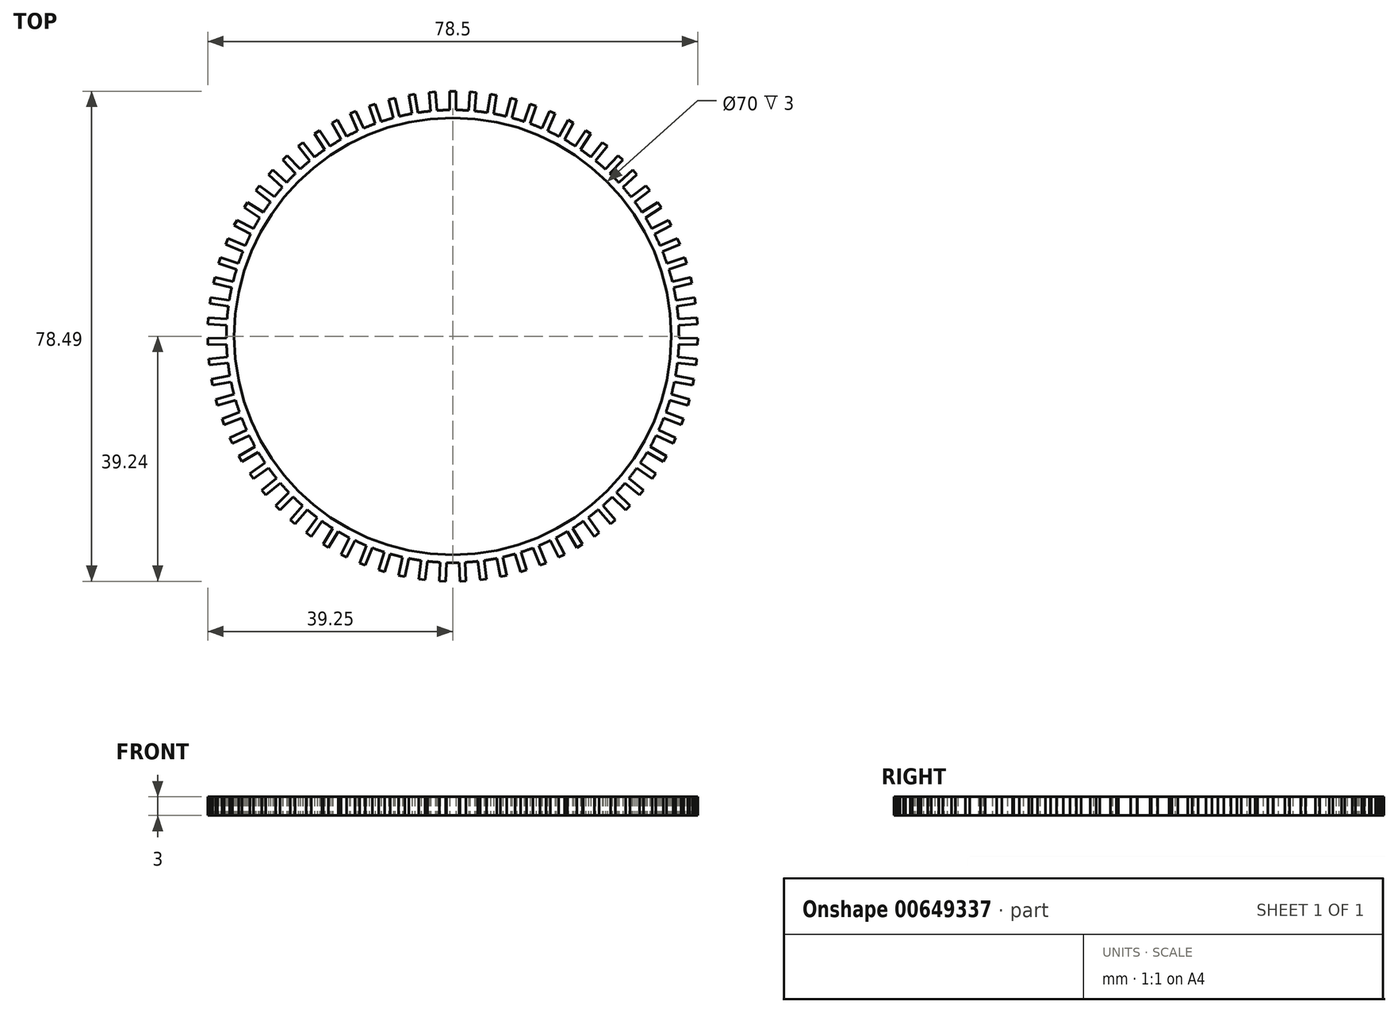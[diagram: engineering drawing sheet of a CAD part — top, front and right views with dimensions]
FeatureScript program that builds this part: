
annotation { "Feature Type Name" : "Feature", "Feature Type Description" : "" }
export const myFeature = defineFeature(function(context is Context, id is Id, definition is map)
    precondition{}
    {
        {
            var Q0;
            Q0=qCreatedBy(makeId("Top.planeOp"),FACE);
            var sketch = newSketch(context, id + "F0", { "sketchPlane" : qUnion([Q0])});
            skCircle(sketch, "E0", {"center": v(0, 0) * mm, "radius": 36.25 * mm});
            skCircle(sketch, "E1", {"center": v(0, 0) * mm, "radius": 35 * mm});
            skLineSegment(sketch, "E2.bottom", {"start": v(0.5, 39.25) * mm, "end": v(-0.5, 39.25) * mm});
            skLineSegment(sketch, "E2.top", {"start": v(0.5, 33.25) * mm, "end": v(-0.5, 33.25) * mm});
            skLineSegment(sketch, "E2.left", {"start": v(0.5, 39.25) * mm, "end": v(0.5, 33.25) * mm});
            skLineSegment(sketch, "E2.right", {"start": v(-0.5, 39.25) * mm, "end": v(-0.5, 33.25) * mm});
            skPoint(sketch, "E2.middle", {"position": v(0, 36.25) * mm});
            skLineSegment(sketch, "E3.1.0", {"start": v(-2.79, 39.15) * mm, "end": v(-3.78, 39.07) * mm});
            skLineSegment(sketch, "E3.1.1", {"start": v(-3.78, 39.07) * mm, "end": v(-3.28, 33.1) * mm});
            skLineSegment(sketch, "E3.1.2", {"start": v(-2.79, 39.15) * mm, "end": v(-2.28, 33.18) * mm});
            skLineSegment(sketch, "E3.2.0", {"start": v(-6.05, 38.78) * mm, "end": v(-7.04, 38.62) * mm});
            skLineSegment(sketch, "E3.2.1", {"start": v(-7.04, 38.62) * mm, "end": v(-6.04, 32.7) * mm});
            skLineSegment(sketch, "E3.2.2", {"start": v(-6.05, 38.78) * mm, "end": v(-5.05, 32.87) * mm});
            skLineSegment(sketch, "E3.3.0", {"start": v(-9.28, 38.14) * mm, "end": v(-10.25, 37.9) * mm});
            skLineSegment(sketch, "E3.3.1", {"start": v(-10.25, 37.9) * mm, "end": v(-8.75, 32.08) * mm});
            skLineSegment(sketch, "E3.3.2", {"start": v(-9.28, 38.14) * mm, "end": v(-7.78, 32.33) * mm});
            skLineSegment(sketch, "E3.4.0", {"start": v(-12.44, 37.23) * mm, "end": v(-13.38, 36.9) * mm});
            skLineSegment(sketch, "E3.4.1", {"start": v(-13.38, 36.9) * mm, "end": v(-11.4, 31.24) * mm});
            skLineSegment(sketch, "E3.4.2", {"start": v(-12.44, 37.23) * mm, "end": v(-10.46, 31.56) * mm});
            skLineSegment(sketch, "E3.5.0", {"start": v(-15.5, 36.06) * mm, "end": v(-16.42, 35.65) * mm});
            skLineSegment(sketch, "E3.5.1", {"start": v(-16.42, 35.65) * mm, "end": v(-13.98, 30.17) * mm});
            skLineSegment(sketch, "E3.5.2", {"start": v(-15.5, 36.06) * mm, "end": v(-13.07, 30.58) * mm});
            skLineSegment(sketch, "E3.6.0", {"start": v(-18.47, 34.64) * mm, "end": v(-19.35, 34.15) * mm});
            skLineSegment(sketch, "E3.6.1", {"start": v(-19.35, 34.15) * mm, "end": v(-16.46, 28.9) * mm});
            skLineSegment(sketch, "E3.6.2", {"start": v(-18.47, 34.64) * mm, "end": v(-15.58, 29.38) * mm});
            skLineSegment(sketch, "E3.7.0", {"start": v(-21.3, 32.97) * mm, "end": v(-22.14, 32.42) * mm});
            skLineSegment(sketch, "E3.7.1", {"start": v(-22.14, 32.42) * mm, "end": v(-18.82, 27.42) * mm});
            skLineSegment(sketch, "E3.7.2", {"start": v(-21.3, 32.97) * mm, "end": v(-17.98, 27.97) * mm});
            skLineSegment(sketch, "E3.8.0", {"start": v(-23.99, 31.07) * mm, "end": v(-24.77, 30.45) * mm});
            skLineSegment(sketch, "E3.8.1", {"start": v(-24.77, 30.45) * mm, "end": v(-21.05, 25.75) * mm});
            skLineSegment(sketch, "E3.8.2", {"start": v(-23.99, 31.07) * mm, "end": v(-20.26, 26.37) * mm});
            skLineSegment(sketch, "E3.9.0", {"start": v(-26.5, 28.95) * mm, "end": v(-27.23, 28.27) * mm});
            skLineSegment(sketch, "E3.9.1", {"start": v(-27.23, 28.27) * mm, "end": v(-23.13, 23.9) * mm});
            skLineSegment(sketch, "E3.9.2", {"start": v(-26.5, 28.95) * mm, "end": v(-22.4, 24.58) * mm});
            skLineSegment(sketch, "E3.10.0", {"start": v(-28.83, 26.63) * mm, "end": v(-29.5, 25.9) * mm});
            skLineSegment(sketch, "E3.10.1", {"start": v(-29.5, 25.9) * mm, "end": v(-25.04, 21.88) * mm});
            skLineSegment(sketch, "E3.10.2", {"start": v(-28.83, 26.63) * mm, "end": v(-24.38, 22.62) * mm});
            skLineSegment(sketch, "E3.11.0", {"start": v(-30.96, 24.13) * mm, "end": v(-31.57, 23.33) * mm});
            skLineSegment(sketch, "E3.11.1", {"start": v(-31.57, 23.33) * mm, "end": v(-26.79, 19.7) * mm});
            skLineSegment(sketch, "E3.11.2", {"start": v(-30.96, 24.13) * mm, "end": v(-26.18, 20.5) * mm});
            skLineSegment(sketch, "E3.12.0", {"start": v(-32.87, 21.45) * mm, "end": v(-33.4, 20.6) * mm});
            skLineSegment(sketch, "E3.12.1", {"start": v(-33.4, 20.6) * mm, "end": v(-28.34, 17.4) * mm});
            skLineSegment(sketch, "E3.12.2", {"start": v(-32.87, 21.45) * mm, "end": v(-27.8, 18.24) * mm});
            skLineSegment(sketch, "E3.13.0", {"start": v(-34.55, 18.63) * mm, "end": v(-35.02, 17.74) * mm});
            skLineSegment(sketch, "E3.13.1", {"start": v(-35.02, 17.74) * mm, "end": v(-29.7, 14.96) * mm});
            skLineSegment(sketch, "E3.13.2", {"start": v(-34.55, 18.63) * mm, "end": v(-29.23, 15.85) * mm});
            skLineSegment(sketch, "E3.14.0", {"start": v(-35.99, 15.67) * mm, "end": v(-36.38, 14.75) * mm});
            skLineSegment(sketch, "E3.14.1", {"start": v(-36.38, 14.75) * mm, "end": v(-30.85, 12.42) * mm});
            skLineSegment(sketch, "E3.14.2", {"start": v(-35.99, 15.67) * mm, "end": v(-30.46, 13.35) * mm});
            skLineSegment(sketch, "E3.15.0", {"start": v(-37.17, 12.6) * mm, "end": v(-37.48, 11.65) * mm});
            skLineSegment(sketch, "E3.15.1", {"start": v(-37.48, 11.65) * mm, "end": v(-31.78, 9.8) * mm});
            skLineSegment(sketch, "E3.15.2", {"start": v(-37.17, 12.6) * mm, "end": v(-31.47, 10.75) * mm});
            skLineSegment(sketch, "E3.16.0", {"start": v(-38.1, 9.45) * mm, "end": v(-38.33, 8.48) * mm});
            skLineSegment(sketch, "E3.16.1", {"start": v(-38.33, 8.48) * mm, "end": v(-32.49, 7.1) * mm});
            skLineSegment(sketch, "E3.16.2", {"start": v(-38.1, 9.45) * mm, "end": v(-32.26, 8.08) * mm});
            skLineSegment(sketch, "E3.17.0", {"start": v(-38.76, 6.23) * mm, "end": v(-38.9, 5.24) * mm});
            skLineSegment(sketch, "E3.17.1", {"start": v(-38.9, 5.24) * mm, "end": v(-32.97, 4.36) * mm});
            skLineSegment(sketch, "E3.17.2", {"start": v(-38.76, 6.23) * mm, "end": v(-32.82, 5.35) * mm});
            skLineSegment(sketch, "E3.18.0", {"start": v(-39.14, 2.96) * mm, "end": v(-39.2, 1.97) * mm});
            skLineSegment(sketch, "E3.18.1", {"start": v(-39.2, 1.97) * mm, "end": v(-33.22, 1.59) * mm});
            skLineSegment(sketch, "E3.18.2", {"start": v(-39.14, 2.96) * mm, "end": v(-33.15, 2.59) * mm});
            skLineSegment(sketch, "E3.19.0", {"start": v(-39.25, -0.32) * mm, "end": v(-39.23, -1.32) * mm});
            skLineSegment(sketch, "E3.19.1", {"start": v(-39.23, -1.32) * mm, "end": v(-33.23, -1.2) * mm});
            skLineSegment(sketch, "E3.19.2", {"start": v(-39.25, -0.32) * mm, "end": v(-33.25, -0.2) * mm});
            skLineSegment(sketch, "E3.20.0", {"start": v(-39.09, -3.6) * mm, "end": v(-38.98, -4.6) * mm});
            skLineSegment(sketch, "E3.20.1", {"start": v(-38.98, -4.6) * mm, "end": v(-33.02, -3.97) * mm});
            skLineSegment(sketch, "E3.20.2", {"start": v(-39.09, -3.6) * mm, "end": v(-33.12, -2.98) * mm});
            skLineSegment(sketch, "E3.21.0", {"start": v(-38.65, -6.86) * mm, "end": v(-38.46, -7.85) * mm});
            skLineSegment(sketch, "E3.21.1", {"start": v(-38.46, -7.85) * mm, "end": v(-32.57, -6.72) * mm});
            skLineSegment(sketch, "E3.21.2", {"start": v(-38.65, -6.86) * mm, "end": v(-32.75, -5.74) * mm});
            skLineSegment(sketch, "E3.22.0", {"start": v(-37.94, -10.07) * mm, "end": v(-37.67, -11.04) * mm});
            skLineSegment(sketch, "E3.22.1", {"start": v(-37.67, -11.04) * mm, "end": v(-31.9, -9.42) * mm});
            skLineSegment(sketch, "E3.22.2", {"start": v(-37.94, -10.07) * mm, "end": v(-32.16, -8.46) * mm});
            skLineSegment(sketch, "E3.23.0", {"start": v(-36.96, -13.21) * mm, "end": v(-36.61, -14.15) * mm});
            skLineSegment(sketch, "E3.23.1", {"start": v(-36.61, -14.15) * mm, "end": v(-31, -12.06) * mm});
            skLineSegment(sketch, "E3.23.2", {"start": v(-36.96, -13.21) * mm, "end": v(-31.34, -11.12) * mm});
            skLineSegment(sketch, "E3.24.0", {"start": v(-35.73, -16.26) * mm, "end": v(-35.3, -17.16) * mm});
            skLineSegment(sketch, "E3.24.1", {"start": v(-35.3, -17.16) * mm, "end": v(-29.87, -14.6) * mm});
            skLineSegment(sketch, "E3.24.2", {"start": v(-35.73, -16.26) * mm, "end": v(-30.3, -13.7) * mm});
            skLineSegment(sketch, "E3.25.0", {"start": v(-34.24, -19.2) * mm, "end": v(-33.74, -20.06) * mm});
            skLineSegment(sketch, "E3.25.1", {"start": v(-33.74, -20.06) * mm, "end": v(-28.55, -17.06) * mm});
            skLineSegment(sketch, "E3.25.2", {"start": v(-34.24, -19.2) * mm, "end": v(-29.05, -16.2) * mm});
            skLineSegment(sketch, "E3.26.0", {"start": v(-32.52, -21.99) * mm, "end": v(-31.94, -22.81) * mm});
            skLineSegment(sketch, "E3.26.1", {"start": v(-31.94, -22.81) * mm, "end": v(-27.02, -19.39) * mm});
            skLineSegment(sketch, "E3.26.2", {"start": v(-32.52, -21.99) * mm, "end": v(-27.59, -18.57) * mm});
            skLineSegment(sketch, "E3.27.0", {"start": v(-30.56, -24.63) * mm, "end": v(-29.92, -25.4) * mm});
            skLineSegment(sketch, "E3.27.1", {"start": v(-29.92, -25.4) * mm, "end": v(-25.3, -21.58) * mm});
            skLineSegment(sketch, "E3.27.2", {"start": v(-30.56, -24.63) * mm, "end": v(-25.94, -20.8) * mm});
            skLineSegment(sketch, "E3.28.0", {"start": v(-28.4, -27.1) * mm, "end": v(-27.7, -27.82) * mm});
            skLineSegment(sketch, "E3.28.1", {"start": v(-27.7, -27.82) * mm, "end": v(-23.4, -23.62) * mm});
            skLineSegment(sketch, "E3.28.2", {"start": v(-28.4, -27.1) * mm, "end": v(-24.1, -22.9) * mm});
            skLineSegment(sketch, "E3.29.0", {"start": v(-26.03, -29.39) * mm, "end": v(-25.27, -30.04) * mm});
            skLineSegment(sketch, "E3.29.1", {"start": v(-25.27, -30.04) * mm, "end": v(-21.35, -25.5) * mm});
            skLineSegment(sketch, "E3.29.2", {"start": v(-26.03, -29.39) * mm, "end": v(-22.1, -24.84) * mm});
            skLineSegment(sketch, "E3.30.0", {"start": v(-23.48, -31.46) * mm, "end": v(-22.67, -32.05) * mm});
            skLineSegment(sketch, "E3.30.1", {"start": v(-22.67, -32.05) * mm, "end": v(-19.14, -27.2) * mm});
            skLineSegment(sketch, "E3.30.2", {"start": v(-23.48, -31.46) * mm, "end": v(-19.95, -26.6) * mm});
            skLineSegment(sketch, "E3.31.0", {"start": v(-20.76, -33.31) * mm, "end": v(-19.9, -33.83) * mm});
            skLineSegment(sketch, "E3.31.1", {"start": v(-19.9, -33.83) * mm, "end": v(-16.8, -28.7) * mm});
            skLineSegment(sketch, "E3.31.2", {"start": v(-20.76, -33.31) * mm, "end": v(-17.65, -28.18) * mm});
            skLineSegment(sketch, "E3.32.0", {"start": v(-17.9, -34.93) * mm, "end": v(-17, -35.38) * mm});
            skLineSegment(sketch, "E3.32.1", {"start": v(-17, -35.38) * mm, "end": v(-14.34, -30) * mm});
            skLineSegment(sketch, "E3.32.2", {"start": v(-17.9, -34.93) * mm, "end": v(-15.23, -29.56) * mm});
            skLineSegment(sketch, "E3.33.0", {"start": v(-14.91, -36.3) * mm, "end": v(-13.98, -36.68) * mm});
            skLineSegment(sketch, "E3.33.1", {"start": v(-13.98, -36.68) * mm, "end": v(-11.78, -31.1) * mm});
            skLineSegment(sketch, "E3.33.2", {"start": v(-14.91, -36.3) * mm, "end": v(-12.7, -30.73) * mm});
            skLineSegment(sketch, "E3.34.0", {"start": v(-11.82, -37.43) * mm, "end": v(-10.87, -37.72) * mm});
            skLineSegment(sketch, "E3.34.1", {"start": v(-10.87, -37.72) * mm, "end": v(-9.13, -31.98) * mm});
            skLineSegment(sketch, "E3.34.2", {"start": v(-11.82, -37.43) * mm, "end": v(-10.09, -31.69) * mm});
            skLineSegment(sketch, "E3.35.0", {"start": v(-8.65, -38.29) * mm, "end": v(-7.67, -38.5) * mm});
            skLineSegment(sketch, "E3.35.1", {"start": v(-7.67, -38.5) * mm, "end": v(-6.42, -32.63) * mm});
            skLineSegment(sketch, "E3.35.2", {"start": v(-8.65, -38.29) * mm, "end": v(-7.4, -32.42) * mm});
            skLineSegment(sketch, "E3.36.0", {"start": v(-5.42, -38.88) * mm, "end": v(-4.42, -39) * mm});
            skLineSegment(sketch, "E3.36.1", {"start": v(-4.42, -39) * mm, "end": v(-3.67, -33.05) * mm});
            skLineSegment(sketch, "E3.36.2", {"start": v(-5.42, -38.88) * mm, "end": v(-4.66, -32.93) * mm});
            skLineSegment(sketch, "E3.37.0", {"start": v(-2.14, -39.2) * mm, "end": v(-1.14, -39.24) * mm});
            skLineSegment(sketch, "E3.37.1", {"start": v(-1.14, -39.24) * mm, "end": v(-0.9, -33.24) * mm});
            skLineSegment(sketch, "E3.37.2", {"start": v(-2.14, -39.2) * mm, "end": v(-1.9, -33.2) * mm});
            skLineSegment(sketch, "E3.38.0", {"start": v(1.14, -39.24) * mm, "end": v(2.14, -39.2) * mm});
            skLineSegment(sketch, "E3.38.1", {"start": v(2.14, -39.2) * mm, "end": v(1.9, -33.2) * mm});
            skLineSegment(sketch, "E3.38.2", {"start": v(1.14, -39.24) * mm, "end": v(0.9, -33.24) * mm});
            skLineSegment(sketch, "E3.39.0", {"start": v(4.42, -39) * mm, "end": v(5.42, -38.88) * mm});
            skLineSegment(sketch, "E3.39.1", {"start": v(5.42, -38.88) * mm, "end": v(4.66, -32.93) * mm});
            skLineSegment(sketch, "E3.39.2", {"start": v(4.42, -39) * mm, "end": v(3.67, -33.05) * mm});
            skLineSegment(sketch, "E3.40.0", {"start": v(7.67, -38.5) * mm, "end": v(8.65, -38.29) * mm});
            skLineSegment(sketch, "E3.40.1", {"start": v(8.65, -38.29) * mm, "end": v(7.4, -32.42) * mm});
            skLineSegment(sketch, "E3.40.2", {"start": v(7.67, -38.5) * mm, "end": v(6.42, -32.63) * mm});
            skLineSegment(sketch, "E3.41.0", {"start": v(10.87, -37.72) * mm, "end": v(11.82, -37.43) * mm});
            skLineSegment(sketch, "E3.41.1", {"start": v(11.82, -37.43) * mm, "end": v(10.09, -31.69) * mm});
            skLineSegment(sketch, "E3.41.2", {"start": v(10.87, -37.72) * mm, "end": v(9.13, -31.98) * mm});
            skLineSegment(sketch, "E3.42.0", {"start": v(13.98, -36.68) * mm, "end": v(14.91, -36.3) * mm});
            skLineSegment(sketch, "E3.42.1", {"start": v(14.91, -36.3) * mm, "end": v(12.7, -30.73) * mm});
            skLineSegment(sketch, "E3.42.2", {"start": v(13.98, -36.68) * mm, "end": v(11.78, -31.1) * mm});
            skLineSegment(sketch, "E3.43.0", {"start": v(17, -35.38) * mm, "end": v(17.9, -34.93) * mm});
            skLineSegment(sketch, "E3.43.1", {"start": v(17.9, -34.93) * mm, "end": v(15.23, -29.56) * mm});
            skLineSegment(sketch, "E3.43.2", {"start": v(17, -35.38) * mm, "end": v(14.34, -30) * mm});
            skLineSegment(sketch, "E3.44.0", {"start": v(19.9, -33.83) * mm, "end": v(20.76, -33.31) * mm});
            skLineSegment(sketch, "E3.44.1", {"start": v(20.76, -33.31) * mm, "end": v(17.65, -28.18) * mm});
            skLineSegment(sketch, "E3.44.2", {"start": v(19.9, -33.83) * mm, "end": v(16.8, -28.7) * mm});
            skLineSegment(sketch, "E3.45.0", {"start": v(22.67, -32.05) * mm, "end": v(23.48, -31.46) * mm});
            skLineSegment(sketch, "E3.45.1", {"start": v(23.48, -31.46) * mm, "end": v(19.95, -26.6) * mm});
            skLineSegment(sketch, "E3.45.2", {"start": v(22.67, -32.05) * mm, "end": v(19.14, -27.2) * mm});
            skLineSegment(sketch, "E3.46.0", {"start": v(25.27, -30.04) * mm, "end": v(26.03, -29.39) * mm});
            skLineSegment(sketch, "E3.46.1", {"start": v(26.03, -29.39) * mm, "end": v(22.1, -24.84) * mm});
            skLineSegment(sketch, "E3.46.2", {"start": v(25.27, -30.04) * mm, "end": v(21.35, -25.5) * mm});
            skLineSegment(sketch, "E3.47.0", {"start": v(27.7, -27.82) * mm, "end": v(28.4, -27.1) * mm});
            skLineSegment(sketch, "E3.47.1", {"start": v(28.4, -27.1) * mm, "end": v(24.1, -22.9) * mm});
            skLineSegment(sketch, "E3.47.2", {"start": v(27.7, -27.82) * mm, "end": v(23.4, -23.62) * mm});
            skLineSegment(sketch, "E3.48.0", {"start": v(29.92, -25.4) * mm, "end": v(30.56, -24.63) * mm});
            skLineSegment(sketch, "E3.48.1", {"start": v(30.56, -24.63) * mm, "end": v(25.94, -20.8) * mm});
            skLineSegment(sketch, "E3.48.2", {"start": v(29.92, -25.4) * mm, "end": v(25.3, -21.58) * mm});
            skLineSegment(sketch, "E3.49.0", {"start": v(31.94, -22.81) * mm, "end": v(32.52, -21.99) * mm});
            skLineSegment(sketch, "E3.49.1", {"start": v(32.52, -21.99) * mm, "end": v(27.59, -18.57) * mm});
            skLineSegment(sketch, "E3.49.2", {"start": v(31.94, -22.81) * mm, "end": v(27.02, -19.39) * mm});
            skLineSegment(sketch, "E3.50.0", {"start": v(33.74, -20.06) * mm, "end": v(34.24, -19.2) * mm});
            skLineSegment(sketch, "E3.50.1", {"start": v(34.24, -19.2) * mm, "end": v(29.05, -16.2) * mm});
            skLineSegment(sketch, "E3.50.2", {"start": v(33.74, -20.06) * mm, "end": v(28.55, -17.06) * mm});
            skLineSegment(sketch, "E3.51.0", {"start": v(35.3, -17.16) * mm, "end": v(35.73, -16.26) * mm});
            skLineSegment(sketch, "E3.51.1", {"start": v(35.73, -16.26) * mm, "end": v(30.3, -13.7) * mm});
            skLineSegment(sketch, "E3.51.2", {"start": v(35.3, -17.16) * mm, "end": v(29.87, -14.6) * mm});
            skLineSegment(sketch, "E3.52.0", {"start": v(36.61, -14.15) * mm, "end": v(36.96, -13.21) * mm});
            skLineSegment(sketch, "E3.52.1", {"start": v(36.96, -13.21) * mm, "end": v(31.34, -11.12) * mm});
            skLineSegment(sketch, "E3.52.2", {"start": v(36.61, -14.15) * mm, "end": v(31, -12.06) * mm});
            skLineSegment(sketch, "E3.53.0", {"start": v(37.67, -11.04) * mm, "end": v(37.94, -10.07) * mm});
            skLineSegment(sketch, "E3.53.1", {"start": v(37.94, -10.07) * mm, "end": v(32.16, -8.46) * mm});
            skLineSegment(sketch, "E3.53.2", {"start": v(37.67, -11.04) * mm, "end": v(31.9, -9.42) * mm});
            skLineSegment(sketch, "E3.54.0", {"start": v(38.46, -7.85) * mm, "end": v(38.65, -6.86) * mm});
            skLineSegment(sketch, "E3.54.1", {"start": v(38.65, -6.86) * mm, "end": v(32.75, -5.74) * mm});
            skLineSegment(sketch, "E3.54.2", {"start": v(38.46, -7.85) * mm, "end": v(32.57, -6.72) * mm});
            skLineSegment(sketch, "E3.55.0", {"start": v(38.98, -4.6) * mm, "end": v(39.09, -3.6) * mm});
            skLineSegment(sketch, "E3.55.1", {"start": v(39.09, -3.6) * mm, "end": v(33.12, -2.98) * mm});
            skLineSegment(sketch, "E3.55.2", {"start": v(38.98, -4.6) * mm, "end": v(33.02, -3.97) * mm});
            skLineSegment(sketch, "E3.56.0", {"start": v(39.23, -1.32) * mm, "end": v(39.25, -0.32) * mm});
            skLineSegment(sketch, "E3.56.1", {"start": v(39.25, -0.32) * mm, "end": v(33.25, -0.2) * mm});
            skLineSegment(sketch, "E3.56.2", {"start": v(39.23, -1.32) * mm, "end": v(33.23, -1.2) * mm});
            skLineSegment(sketch, "E3.57.0", {"start": v(39.2, 1.97) * mm, "end": v(39.14, 2.96) * mm});
            skLineSegment(sketch, "E3.57.1", {"start": v(39.14, 2.96) * mm, "end": v(33.15, 2.59) * mm});
            skLineSegment(sketch, "E3.57.2", {"start": v(39.2, 1.97) * mm, "end": v(33.22, 1.59) * mm});
            skLineSegment(sketch, "E3.58.0", {"start": v(38.9, 5.24) * mm, "end": v(38.76, 6.23) * mm});
            skLineSegment(sketch, "E3.58.1", {"start": v(38.76, 6.23) * mm, "end": v(32.82, 5.35) * mm});
            skLineSegment(sketch, "E3.58.2", {"start": v(38.9, 5.24) * mm, "end": v(32.97, 4.36) * mm});
            skLineSegment(sketch, "E3.59.0", {"start": v(38.33, 8.48) * mm, "end": v(38.1, 9.45) * mm});
            skLineSegment(sketch, "E3.59.1", {"start": v(38.1, 9.45) * mm, "end": v(32.26, 8.08) * mm});
            skLineSegment(sketch, "E3.59.2", {"start": v(38.33, 8.48) * mm, "end": v(32.49, 7.1) * mm});
            skLineSegment(sketch, "E3.60.0", {"start": v(37.48, 11.65) * mm, "end": v(37.17, 12.6) * mm});
            skLineSegment(sketch, "E3.60.1", {"start": v(37.17, 12.6) * mm, "end": v(31.47, 10.75) * mm});
            skLineSegment(sketch, "E3.60.2", {"start": v(37.48, 11.65) * mm, "end": v(31.78, 9.8) * mm});
            skLineSegment(sketch, "E3.61.0", {"start": v(36.38, 14.75) * mm, "end": v(35.99, 15.67) * mm});
            skLineSegment(sketch, "E3.61.1", {"start": v(35.99, 15.67) * mm, "end": v(30.46, 13.35) * mm});
            skLineSegment(sketch, "E3.61.2", {"start": v(36.38, 14.75) * mm, "end": v(30.85, 12.42) * mm});
            skLineSegment(sketch, "E3.62.0", {"start": v(35.02, 17.74) * mm, "end": v(34.55, 18.63) * mm});
            skLineSegment(sketch, "E3.62.1", {"start": v(34.55, 18.63) * mm, "end": v(29.23, 15.85) * mm});
            skLineSegment(sketch, "E3.62.2", {"start": v(35.02, 17.74) * mm, "end": v(29.7, 14.96) * mm});
            skLineSegment(sketch, "E3.63.0", {"start": v(33.4, 20.6) * mm, "end": v(32.87, 21.45) * mm});
            skLineSegment(sketch, "E3.63.1", {"start": v(32.87, 21.45) * mm, "end": v(27.8, 18.24) * mm});
            skLineSegment(sketch, "E3.63.2", {"start": v(33.4, 20.6) * mm, "end": v(28.34, 17.4) * mm});
            skLineSegment(sketch, "E3.64.0", {"start": v(31.57, 23.33) * mm, "end": v(30.96, 24.13) * mm});
            skLineSegment(sketch, "E3.64.1", {"start": v(30.96, 24.13) * mm, "end": v(26.18, 20.5) * mm});
            skLineSegment(sketch, "E3.64.2", {"start": v(31.57, 23.33) * mm, "end": v(26.79, 19.7) * mm});
            skLineSegment(sketch, "E3.65.0", {"start": v(29.5, 25.9) * mm, "end": v(28.83, 26.63) * mm});
            skLineSegment(sketch, "E3.65.1", {"start": v(28.83, 26.63) * mm, "end": v(24.38, 22.62) * mm});
            skLineSegment(sketch, "E3.65.2", {"start": v(29.5, 25.9) * mm, "end": v(25.04, 21.88) * mm});
            skLineSegment(sketch, "E3.66.0", {"start": v(27.23, 28.27) * mm, "end": v(26.5, 28.95) * mm});
            skLineSegment(sketch, "E3.66.1", {"start": v(26.5, 28.95) * mm, "end": v(22.4, 24.58) * mm});
            skLineSegment(sketch, "E3.66.2", {"start": v(27.23, 28.27) * mm, "end": v(23.13, 23.9) * mm});
            skLineSegment(sketch, "E3.67.0", {"start": v(24.77, 30.45) * mm, "end": v(23.99, 31.07) * mm});
            skLineSegment(sketch, "E3.67.1", {"start": v(23.99, 31.07) * mm, "end": v(20.26, 26.37) * mm});
            skLineSegment(sketch, "E3.67.2", {"start": v(24.77, 30.45) * mm, "end": v(21.05, 25.75) * mm});
            skLineSegment(sketch, "E3.68.0", {"start": v(22.14, 32.42) * mm, "end": v(21.3, 32.97) * mm});
            skLineSegment(sketch, "E3.68.1", {"start": v(21.3, 32.97) * mm, "end": v(17.98, 27.97) * mm});
            skLineSegment(sketch, "E3.68.2", {"start": v(22.14, 32.42) * mm, "end": v(18.82, 27.42) * mm});
            skLineSegment(sketch, "E3.69.0", {"start": v(19.35, 34.15) * mm, "end": v(18.47, 34.64) * mm});
            skLineSegment(sketch, "E3.69.1", {"start": v(18.47, 34.64) * mm, "end": v(15.58, 29.38) * mm});
            skLineSegment(sketch, "E3.69.2", {"start": v(19.35, 34.15) * mm, "end": v(16.46, 28.9) * mm});
            skLineSegment(sketch, "E3.70.0", {"start": v(16.42, 35.65) * mm, "end": v(15.5, 36.06) * mm});
            skLineSegment(sketch, "E3.70.1", {"start": v(15.5, 36.06) * mm, "end": v(13.07, 30.58) * mm});
            skLineSegment(sketch, "E3.70.2", {"start": v(16.42, 35.65) * mm, "end": v(13.98, 30.17) * mm});
            skLineSegment(sketch, "E3.71.0", {"start": v(13.38, 36.9) * mm, "end": v(12.44, 37.23) * mm});
            skLineSegment(sketch, "E3.71.1", {"start": v(12.44, 37.23) * mm, "end": v(10.46, 31.56) * mm});
            skLineSegment(sketch, "E3.71.2", {"start": v(13.38, 36.9) * mm, "end": v(11.4, 31.24) * mm});
            skLineSegment(sketch, "E3.72.0", {"start": v(10.25, 37.9) * mm, "end": v(9.28, 38.14) * mm});
            skLineSegment(sketch, "E3.72.1", {"start": v(9.28, 38.14) * mm, "end": v(7.78, 32.33) * mm});
            skLineSegment(sketch, "E3.72.2", {"start": v(10.25, 37.9) * mm, "end": v(8.75, 32.08) * mm});
            skLineSegment(sketch, "E3.73.0", {"start": v(7.04, 38.62) * mm, "end": v(6.05, 38.78) * mm});
            skLineSegment(sketch, "E3.73.1", {"start": v(6.05, 38.78) * mm, "end": v(5.05, 32.87) * mm});
            skLineSegment(sketch, "E3.73.2", {"start": v(7.04, 38.62) * mm, "end": v(6.04, 32.7) * mm});
            skLineSegment(sketch, "E3.74.0", {"start": v(3.78, 39.07) * mm, "end": v(2.79, 39.15) * mm});
            skLineSegment(sketch, "E3.74.1", {"start": v(2.79, 39.15) * mm, "end": v(2.28, 33.18) * mm});
            skLineSegment(sketch, "E3.74.2", {"start": v(3.78, 39.07) * mm, "end": v(3.28, 33.1) * mm});
            skCircle(sketch, "E4", {"center": v(0, 0) * mm, "radius": 41.25 * mm});
            skCircle(sketch, "E5", {"center": v(0, 0) * mm, "radius": 44.56 * mm});
            skSolve(sketch);
        }
        {
            var Q0;
            {var subQ0=sQuery(id+"F0.wireOp",EDGE,"E3.62.2");var subQ1=sQuery(id+"F0.wireOp",EDGE,"E1");var subQ2=makeQuery(id+"F0.imprint","INTERSECT",VERTEX,{"derivedFrom":[subQ1,subQ0]});Q0=makeQuery(id+"F0.imprint","IMPRINT",FACE,{"disambiguationData":[TD([[makeQuery(id+"F0.imprint","IMPRINT",EDGE,{"disambiguationData":[TD([[subQ2,-1.0]])],"derivedFrom":subQ1}),-1.0]])]});}
            var Q1;
            {var subQ0=sQuery(id+"F0.wireOp",EDGE,"E3.46.2");var subQ1=sQuery(id+"F0.wireOp",EDGE,"E1");var subQ2=makeQuery(id+"F0.imprint","INTERSECT",VERTEX,{"derivedFrom":[subQ1,subQ0]});Q1=makeQuery(id+"F0.imprint","IMPRINT",FACE,{"disambiguationData":[TD([[makeQuery(id+"F0.imprint","IMPRINT",EDGE,{"disambiguationData":[TD([[subQ2,-1.0]])],"derivedFrom":subQ1}),-1.0]])]});}
            var Q2;
            {var subQ0=sQuery(id+"F0.wireOp",EDGE,"E3.30.2");var subQ1=sQuery(id+"F0.wireOp",EDGE,"E1");var subQ2=makeQuery(id+"F0.imprint","INTERSECT",VERTEX,{"derivedFrom":[subQ1,subQ0]});Q2=makeQuery(id+"F0.imprint","IMPRINT",FACE,{"disambiguationData":[TD([[makeQuery(id+"F0.imprint","IMPRINT",EDGE,{"disambiguationData":[TD([[subQ2,-1.0]])],"derivedFrom":subQ1}),-1.0]])]});}
            var Q3;
            {var subQ0=sQuery(id+"F0.wireOp",EDGE,"E3.14.2");var subQ1=sQuery(id+"F0.wireOp",EDGE,"E1");var subQ2=makeQuery(id+"F0.imprint","INTERSECT",VERTEX,{"derivedFrom":[subQ1,subQ0]});Q3=makeQuery(id+"F0.imprint","IMPRINT",FACE,{"disambiguationData":[TD([[makeQuery(id+"F0.imprint","IMPRINT",EDGE,{"disambiguationData":[TD([[subQ2,-1.0]])],"derivedFrom":subQ1}),-1.0]])]});}
            var Q4;
            {var subQ0=sQuery(id+"F0.wireOp",EDGE,"E3.31.0");Q4=makeQuery(id+"F0.imprint","IMPRINT",FACE,{"disambiguationData":[TD([[makeQuery(id+"F0.imprint","IMPRINT",EDGE,{"derivedFrom":subQ0}),1.0]])]});}
            var Q5;
            {var subQ0=sQuery(id+"F0.wireOp",EDGE,"E3.95.0");Q5=makeQuery(id+"F0.imprint","IMPRINT",FACE,{"disambiguationData":[TD([[makeQuery(id+"F0.imprint","IMPRINT",EDGE,{"derivedFrom":subQ0}),1.0]])]});}
            var Q6;
            {var subQ0=sQuery(id+"F0.wireOp",EDGE,"E3.79.0");Q6=makeQuery(id+"F0.imprint","IMPRINT",FACE,{"disambiguationData":[TD([[makeQuery(id+"F0.imprint","IMPRINT",EDGE,{"derivedFrom":subQ0}),1.0]])]});}
            var Q7;
            {var subQ0=sQuery(id+"F0.wireOp",EDGE,"E3.63.0");Q7=makeQuery(id+"F0.imprint","IMPRINT",FACE,{"disambiguationData":[TD([[makeQuery(id+"F0.imprint","IMPRINT",EDGE,{"derivedFrom":subQ0}),1.0]])]});}
            var Q8;
            {var subQ0=sQuery(id+"F0.wireOp",EDGE,"E3.47.0");Q8=makeQuery(id+"F0.imprint","IMPRINT",FACE,{"disambiguationData":[TD([[makeQuery(id+"F0.imprint","IMPRINT",EDGE,{"derivedFrom":subQ0}),1.0]])]});}
            var Q9;
            {var subQ0=sQuery(id+"F0.wireOp",EDGE,"E3.33.1");var subQ1=sQuery(id+"F0.wireOp",EDGE,"E1");var subQ2=makeQuery(id+"F0.imprint","INTERSECT",VERTEX,{"derivedFrom":[subQ1,subQ0]});Q9=makeQuery(id+"F0.imprint","IMPRINT",FACE,{"disambiguationData":[TD([[makeQuery(id+"F0.imprint","IMPRINT",EDGE,{"disambiguationData":[TD([[subQ2,-1.0]])],"derivedFrom":subQ1}),-1.0]])]});}
            var Q10;
            {var subQ0=sQuery(id+"F0.wireOp",EDGE,"E3.17.1");var subQ1=sQuery(id+"F0.wireOp",EDGE,"E1");var subQ2=makeQuery(id+"F0.imprint","INTERSECT",VERTEX,{"derivedFrom":[subQ1,subQ0]});Q10=makeQuery(id+"F0.imprint","IMPRINT",FACE,{"disambiguationData":[TD([[makeQuery(id+"F0.imprint","IMPRINT",EDGE,{"disambiguationData":[TD([[subQ2,-1.0]])],"derivedFrom":subQ1}),-1.0]])]});}
            var Q11;
            {var subQ0=sQuery(id+"F0.wireOp",EDGE,"E3.85.1");var subQ1=sQuery(id+"F0.wireOp",EDGE,"E1");var subQ2=makeQuery(id+"F0.imprint","INTERSECT",VERTEX,{"derivedFrom":[subQ1,subQ0]});Q11=makeQuery(id+"F0.imprint","IMPRINT",FACE,{"disambiguationData":[TD([[makeQuery(id+"F0.imprint","IMPRINT",EDGE,{"disambiguationData":[TD([[subQ2,-1.0]])],"derivedFrom":subQ1}),-1.0]])]});}
            var Q12;
            {var subQ0=sQuery(id+"F0.wireOp",EDGE,"E3.82.2");var subQ1=sQuery(id+"F0.wireOp",EDGE,"E1");var subQ2=makeQuery(id+"F0.imprint","INTERSECT",VERTEX,{"derivedFrom":[subQ1,subQ0]});Q12=makeQuery(id+"F0.imprint","IMPRINT",FACE,{"disambiguationData":[TD([[makeQuery(id+"F0.imprint","IMPRINT",EDGE,{"disambiguationData":[TD([[subQ2,-1.0]])],"derivedFrom":subQ1}),-1.0]])]});}
            var Q13;
            {var subQ0=sQuery(id+"F0.wireOp",EDGE,"E3.65.1");var subQ1=sQuery(id+"F0.wireOp",EDGE,"E1");var subQ2=makeQuery(id+"F0.imprint","INTERSECT",VERTEX,{"derivedFrom":[subQ1,subQ0]});Q13=makeQuery(id+"F0.imprint","IMPRINT",FACE,{"disambiguationData":[TD([[makeQuery(id+"F0.imprint","IMPRINT",EDGE,{"disambiguationData":[TD([[subQ2,-1.0]])],"derivedFrom":subQ1}),-1.0]])]});}
            var Q14;
            {var subQ0=sQuery(id+"F0.wireOp",EDGE,"E3.49.1");var subQ1=sQuery(id+"F0.wireOp",EDGE,"E1");var subQ2=makeQuery(id+"F0.imprint","INTERSECT",VERTEX,{"derivedFrom":[subQ1,subQ0]});Q14=makeQuery(id+"F0.imprint","IMPRINT",FACE,{"disambiguationData":[TD([[makeQuery(id+"F0.imprint","IMPRINT",EDGE,{"disambiguationData":[TD([[subQ2,-1.0]])],"derivedFrom":subQ1}),-1.0]])]});}
            var Q15;
            {var subQ0=sQuery(id+"F0.wireOp",EDGE,"E3.77.0");Q15=makeQuery(id+"F0.imprint","IMPRINT",FACE,{"disambiguationData":[TD([[makeQuery(id+"F0.imprint","IMPRINT",EDGE,{"derivedFrom":subQ0}),1.0]])]});}
            var Q16;
            {var subQ0=sQuery(id+"F0.wireOp",EDGE,"E3.61.0");Q16=makeQuery(id+"F0.imprint","IMPRINT",FACE,{"disambiguationData":[TD([[makeQuery(id+"F0.imprint","IMPRINT",EDGE,{"derivedFrom":subQ0}),1.0]])]});}
            var Q17;
            {var subQ0=sQuery(id+"F0.wireOp",EDGE,"E3.45.0");Q17=makeQuery(id+"F0.imprint","IMPRINT",FACE,{"disambiguationData":[TD([[makeQuery(id+"F0.imprint","IMPRINT",EDGE,{"derivedFrom":subQ0}),1.0]])]});}
            var Q18;
            {var subQ0=sQuery(id+"F0.wireOp",EDGE,"E3.15.1");var subQ1=sQuery(id+"F0.wireOp",EDGE,"E1");var subQ2=makeQuery(id+"F0.imprint","INTERSECT",VERTEX,{"derivedFrom":[subQ1,subQ0]});Q18=makeQuery(id+"F0.imprint","IMPRINT",FACE,{"disambiguationData":[TD([[makeQuery(id+"F0.imprint","IMPRINT",EDGE,{"disambiguationData":[TD([[subQ2,-1.0]])],"derivedFrom":subQ1}),-1.0]])]});}
            var Q19;
            {var subQ0=sQuery(id+"F0.wireOp",EDGE,"E3.93.0");Q19=makeQuery(id+"F0.imprint","IMPRINT",FACE,{"disambiguationData":[TD([[makeQuery(id+"F0.imprint","IMPRINT",EDGE,{"derivedFrom":subQ0}),1.0]])]});}
            var Q20;
            {var subQ0=sQuery(id+"F0.wireOp",EDGE,"E3.47.1");var subQ1=sQuery(id+"F0.wireOp",EDGE,"E1");var subQ2=makeQuery(id+"F0.imprint","INTERSECT",VERTEX,{"derivedFrom":[subQ1,subQ0]});Q20=makeQuery(id+"F0.imprint","IMPRINT",FACE,{"disambiguationData":[TD([[makeQuery(id+"F0.imprint","IMPRINT",EDGE,{"disambiguationData":[TD([[subQ2,-1.0]])],"derivedFrom":subQ1}),-1.0]])]});}
            var Q21;
            {var subQ0=sQuery(id+"F0.wireOp",EDGE,"E3.31.1");var subQ1=sQuery(id+"F0.wireOp",EDGE,"E1");var subQ2=makeQuery(id+"F0.imprint","INTERSECT",VERTEX,{"derivedFrom":[subQ1,subQ0]});Q21=makeQuery(id+"F0.imprint","IMPRINT",FACE,{"disambiguationData":[TD([[makeQuery(id+"F0.imprint","IMPRINT",EDGE,{"disambiguationData":[TD([[subQ2,-1.0]])],"derivedFrom":subQ1}),-1.0]])]});}
            var Q22;
            {var subQ0=sQuery(id+"F0.wireOp",EDGE,"E3.96.2");var subQ1=sQuery(id+"F0.wireOp",EDGE,"E1");var subQ2=makeQuery(id+"F0.imprint","INTERSECT",VERTEX,{"derivedFrom":[subQ1,subQ0]});Q22=makeQuery(id+"F0.imprint","IMPRINT",FACE,{"disambiguationData":[TD([[makeQuery(id+"F0.imprint","IMPRINT",EDGE,{"disambiguationData":[TD([[subQ2,-1.0]])],"derivedFrom":subQ1}),-1.0]])]});}
            var Q23;
            {var subQ0=sQuery(id+"F0.wireOp",EDGE,"E3.78.0");Q23=makeQuery(id+"F0.imprint","IMPRINT",FACE,{"disambiguationData":[TD([[makeQuery(id+"F0.imprint","IMPRINT",EDGE,{"derivedFrom":subQ0}),1.0]])]});}
            var Q24;
            {var subQ0=sQuery(id+"F0.wireOp",EDGE,"E3.62.0");Q24=makeQuery(id+"F0.imprint","IMPRINT",FACE,{"disambiguationData":[TD([[makeQuery(id+"F0.imprint","IMPRINT",EDGE,{"derivedFrom":subQ0}),1.0]])]});}
            var Q25;
            {var subQ0=sQuery(id+"F0.wireOp",EDGE,"E3.30.0");Q25=makeQuery(id+"F0.imprint","IMPRINT",FACE,{"disambiguationData":[TD([[makeQuery(id+"F0.imprint","IMPRINT",EDGE,{"derivedFrom":subQ0}),1.0]])]});}
            var Q26;
            {var subQ0=sQuery(id+"F0.wireOp",EDGE,"E3.16.1");var subQ1=sQuery(id+"F0.wireOp",EDGE,"E1");var subQ2=makeQuery(id+"F0.imprint","INTERSECT",VERTEX,{"derivedFrom":[subQ1,subQ0]});Q26=makeQuery(id+"F0.imprint","IMPRINT",FACE,{"disambiguationData":[TD([[makeQuery(id+"F0.imprint","IMPRINT",EDGE,{"disambiguationData":[TD([[subQ2,-1.0]])],"derivedFrom":subQ1}),-1.0]])]});}
            var Q27;
            {var subQ0=sQuery(id+"F0.wireOp",EDGE,"E3.84.1");var subQ1=sQuery(id+"F0.wireOp",EDGE,"E1");var subQ2=makeQuery(id+"F0.imprint","INTERSECT",VERTEX,{"derivedFrom":[subQ1,subQ0]});Q27=makeQuery(id+"F0.imprint","IMPRINT",FACE,{"disambiguationData":[TD([[makeQuery(id+"F0.imprint","IMPRINT",EDGE,{"disambiguationData":[TD([[subQ2,-1.0]])],"derivedFrom":subQ1}),-1.0]])]});}
            var Q28;
            {var subQ0=sQuery(id+"F0.wireOp",EDGE,"E3.94.0");Q28=makeQuery(id+"F0.imprint","IMPRINT",FACE,{"disambiguationData":[TD([[makeQuery(id+"F0.imprint","IMPRINT",EDGE,{"derivedFrom":subQ0}),1.0]])]});}
            var Q29;
            {var subQ0=sQuery(id+"F0.wireOp",EDGE,"E3.64.1");var subQ1=sQuery(id+"F0.wireOp",EDGE,"E1");var subQ2=makeQuery(id+"F0.imprint","INTERSECT",VERTEX,{"derivedFrom":[subQ1,subQ0]});Q29=makeQuery(id+"F0.imprint","IMPRINT",FACE,{"disambiguationData":[TD([[makeQuery(id+"F0.imprint","IMPRINT",EDGE,{"disambiguationData":[TD([[subQ2,-1.0]])],"derivedFrom":subQ1}),-1.0]])]});}
            var Q30;
            {var subQ0=sQuery(id+"F0.wireOp",EDGE,"E3.32.1");var subQ1=sQuery(id+"F0.wireOp",EDGE,"E1");var subQ2=makeQuery(id+"F0.imprint","INTERSECT",VERTEX,{"derivedFrom":[subQ1,subQ0]});Q30=makeQuery(id+"F0.imprint","IMPRINT",FACE,{"disambiguationData":[TD([[makeQuery(id+"F0.imprint","IMPRINT",EDGE,{"disambiguationData":[TD([[subQ2,-1.0]])],"derivedFrom":subQ1}),-1.0]])]});}
            var Q31;
            {var subQ0=sQuery(id+"F0.wireOp",EDGE,"E3.45.2");var subQ1=sQuery(id+"F0.wireOp",EDGE,"E1");var subQ2=makeQuery(id+"F0.imprint","INTERSECT",VERTEX,{"derivedFrom":[subQ1,subQ0]});Q31=makeQuery(id+"F0.imprint","IMPRINT",FACE,{"disambiguationData":[TD([[makeQuery(id+"F0.imprint","IMPRINT",EDGE,{"disambiguationData":[TD([[subQ2,-1.0]])],"derivedFrom":subQ1}),-1.0]])]});}
            var Q32;
            {var subQ0=sQuery(id+"F0.wireOp",EDGE,"E3.29.2");var subQ1=sQuery(id+"F0.wireOp",EDGE,"E1");var subQ2=makeQuery(id+"F0.imprint","INTERSECT",VERTEX,{"derivedFrom":[subQ1,subQ0]});Q32=makeQuery(id+"F0.imprint","IMPRINT",FACE,{"disambiguationData":[TD([[makeQuery(id+"F0.imprint","IMPRINT",EDGE,{"disambiguationData":[TD([[subQ2,-1.0]])],"derivedFrom":subQ1}),-1.0]])]});}
            var Q33;
            {var subQ0=sQuery(id+"F0.wireOp",EDGE,"E3.13.2");var subQ1=sQuery(id+"F0.wireOp",EDGE,"E1");var subQ2=makeQuery(id+"F0.imprint","INTERSECT",VERTEX,{"derivedFrom":[subQ1,subQ0]});Q33=makeQuery(id+"F0.imprint","IMPRINT",FACE,{"disambiguationData":[TD([[makeQuery(id+"F0.imprint","IMPRINT",EDGE,{"disambiguationData":[TD([[subQ2,-1.0]])],"derivedFrom":subQ1}),-1.0]])]});}
            var Q34;
            {var subQ0=sQuery(id+"F0.wireOp",EDGE,"E3.97.2");var subQ1=sQuery(id+"F0.wireOp",EDGE,"E1");var subQ2=makeQuery(id+"F0.imprint","INTERSECT",VERTEX,{"derivedFrom":[subQ1,subQ0]});Q34=makeQuery(id+"F0.imprint","IMPRINT",FACE,{"disambiguationData":[TD([[makeQuery(id+"F0.imprint","IMPRINT",EDGE,{"disambiguationData":[TD([[subQ2,-1.0]])],"derivedFrom":subQ1}),-1.0]])]});}
            var Q35;
            {var subQ0=sQuery(id+"F0.wireOp",EDGE,"E3.16.0");Q35=makeQuery(id+"F0.imprint","IMPRINT",FACE,{"disambiguationData":[TD([[makeQuery(id+"F0.imprint","IMPRINT",EDGE,{"derivedFrom":subQ0}),1.0]])]});}
            var Q36;
            {var subQ0=sQuery(id+"F0.wireOp",EDGE,"E3.80.0");Q36=makeQuery(id+"F0.imprint","IMPRINT",FACE,{"disambiguationData":[TD([[makeQuery(id+"F0.imprint","IMPRINT",EDGE,{"derivedFrom":subQ0}),1.0]])]});}
            var Q37;
            {var subQ0=sQuery(id+"F0.wireOp",EDGE,"E3.64.0");Q37=makeQuery(id+"F0.imprint","IMPRINT",FACE,{"disambiguationData":[TD([[makeQuery(id+"F0.imprint","IMPRINT",EDGE,{"derivedFrom":subQ0}),1.0]])]});}
            var Q38;
            {var subQ0=sQuery(id+"F0.wireOp",EDGE,"E3.18.1");var subQ1=sQuery(id+"F0.wireOp",EDGE,"E1");var subQ2=makeQuery(id+"F0.imprint","INTERSECT",VERTEX,{"derivedFrom":[subQ1,subQ0]});Q38=makeQuery(id+"F0.imprint","IMPRINT",FACE,{"disambiguationData":[TD([[makeQuery(id+"F0.imprint","IMPRINT",EDGE,{"disambiguationData":[TD([[subQ2,-1.0]])],"derivedFrom":subQ1}),-1.0]])]});}
            var Q39;
            {var subQ0=sQuery(id+"F0.wireOp",EDGE,"E3.2.1");var subQ1=sQuery(id+"F0.wireOp",EDGE,"E1");var subQ2=makeQuery(id+"F0.imprint","INTERSECT",VERTEX,{"derivedFrom":[subQ1,subQ0]});Q39=makeQuery(id+"F0.imprint","IMPRINT",FACE,{"disambiguationData":[TD([[makeQuery(id+"F0.imprint","IMPRINT",EDGE,{"disambiguationData":[TD([[subQ2,-1.0]])],"derivedFrom":subQ1}),-1.0]])]});}
            var Q40;
            {var subQ0=sQuery(id+"F0.wireOp",EDGE,"E3.96.0");Q40=makeQuery(id+"F0.imprint","IMPRINT",FACE,{"disambiguationData":[TD([[makeQuery(id+"F0.imprint","IMPRINT",EDGE,{"derivedFrom":subQ0}),1.0]])]});}
            var Q41;
            {var subQ0=sQuery(id+"F0.wireOp",EDGE,"E3.66.1");var subQ1=sQuery(id+"F0.wireOp",EDGE,"E1");var subQ2=makeQuery(id+"F0.imprint","INTERSECT",VERTEX,{"derivedFrom":[subQ1,subQ0]});Q41=makeQuery(id+"F0.imprint","IMPRINT",FACE,{"disambiguationData":[TD([[makeQuery(id+"F0.imprint","IMPRINT",EDGE,{"disambiguationData":[TD([[subQ2,-1.0]])],"derivedFrom":subQ1}),-1.0]])]});}
            var Q42;
            {var subQ0=sQuery(id+"F0.wireOp",EDGE,"E3.50.1");var subQ1=sQuery(id+"F0.wireOp",EDGE,"E1");var subQ2=makeQuery(id+"F0.imprint","INTERSECT",VERTEX,{"derivedFrom":[subQ1,subQ0]});Q42=makeQuery(id+"F0.imprint","IMPRINT",FACE,{"disambiguationData":[TD([[makeQuery(id+"F0.imprint","IMPRINT",EDGE,{"disambiguationData":[TD([[subQ2,-1.0]])],"derivedFrom":subQ1}),-1.0]])]});}
            var Q43;
            {var subQ0=sQuery(id+"F0.wireOp",EDGE,"E3.34.1");var subQ1=sQuery(id+"F0.wireOp",EDGE,"E1");var subQ2=makeQuery(id+"F0.imprint","INTERSECT",VERTEX,{"derivedFrom":[subQ1,subQ0]});Q43=makeQuery(id+"F0.imprint","IMPRINT",FACE,{"disambiguationData":[TD([[makeQuery(id+"F0.imprint","IMPRINT",EDGE,{"disambiguationData":[TD([[subQ2,-1.0]])],"derivedFrom":subQ1}),-1.0]])]});}
            var Q44;
            {var subQ0=sQuery(id+"F0.wireOp",EDGE,"E3.99.2");var subQ1=sQuery(id+"F0.wireOp",EDGE,"E1");var subQ2=makeQuery(id+"F0.imprint","INTERSECT",VERTEX,{"derivedFrom":[subQ1,subQ0]});Q44=makeQuery(id+"F0.imprint","IMPRINT",FACE,{"disambiguationData":[TD([[makeQuery(id+"F0.imprint","IMPRINT",EDGE,{"disambiguationData":[TD([[subQ2,-1.0]])],"derivedFrom":subQ1}),-1.0]])]});}
            var Q45;
            {var subQ0=sQuery(id+"F0.wireOp",EDGE,"E3.17.0");Q45=makeQuery(id+"F0.imprint","IMPRINT",FACE,{"disambiguationData":[TD([[makeQuery(id+"F0.imprint","IMPRINT",EDGE,{"derivedFrom":subQ0}),1.0]])]});}
            var Q46;
            {var subQ0=sQuery(id+"F0.wireOp",EDGE,"E3.81.0");Q46=makeQuery(id+"F0.imprint","IMPRINT",FACE,{"disambiguationData":[TD([[makeQuery(id+"F0.imprint","IMPRINT",EDGE,{"derivedFrom":subQ0}),1.0]])]});}
            var Q47;
            {var subQ0=sQuery(id+"F0.wireOp",EDGE,"E3.65.0");Q47=makeQuery(id+"F0.imprint","IMPRINT",FACE,{"disambiguationData":[TD([[makeQuery(id+"F0.imprint","IMPRINT",EDGE,{"derivedFrom":subQ0}),1.0]])]});}
            var Q48;
            {var subQ0=sQuery(id+"F0.wireOp",EDGE,"E3.49.0");Q48=makeQuery(id+"F0.imprint","IMPRINT",FACE,{"disambiguationData":[TD([[makeQuery(id+"F0.imprint","IMPRINT",EDGE,{"derivedFrom":subQ0}),1.0]])]});}
            var Q49;
            {var subQ0=sQuery(id+"F0.wireOp",EDGE,"E3.19.1");var subQ1=sQuery(id+"F0.wireOp",EDGE,"E1");var subQ2=makeQuery(id+"F0.imprint","INTERSECT",VERTEX,{"derivedFrom":[subQ1,subQ0]});Q49=makeQuery(id+"F0.imprint","IMPRINT",FACE,{"disambiguationData":[TD([[makeQuery(id+"F0.imprint","IMPRINT",EDGE,{"disambiguationData":[TD([[subQ2,-1.0]])],"derivedFrom":subQ1}),-1.0]])]});}
            var Q50;
            {var subQ0=sQuery(id+"F0.wireOp",EDGE,"E3.3.1");var subQ1=sQuery(id+"F0.wireOp",EDGE,"E1");var subQ2=makeQuery(id+"F0.imprint","INTERSECT",VERTEX,{"derivedFrom":[subQ1,subQ0]});Q50=makeQuery(id+"F0.imprint","IMPRINT",FACE,{"disambiguationData":[TD([[makeQuery(id+"F0.imprint","IMPRINT",EDGE,{"disambiguationData":[TD([[subQ2,-1.0]])],"derivedFrom":subQ1}),-1.0]])]});}
            var Q51;
            {var subQ0=sQuery(id+"F0.wireOp",EDGE,"E3.87.1");var subQ1=sQuery(id+"F0.wireOp",EDGE,"E1");var subQ2=makeQuery(id+"F0.imprint","INTERSECT",VERTEX,{"derivedFrom":[subQ1,subQ0]});Q51=makeQuery(id+"F0.imprint","IMPRINT",FACE,{"disambiguationData":[TD([[makeQuery(id+"F0.imprint","IMPRINT",EDGE,{"disambiguationData":[TD([[subQ2,-1.0]])],"derivedFrom":subQ1}),-1.0]])]});}
            var Q52;
            {var subQ0=sQuery(id+"F0.wireOp",EDGE,"E3.97.0");Q52=makeQuery(id+"F0.imprint","IMPRINT",FACE,{"disambiguationData":[TD([[makeQuery(id+"F0.imprint","IMPRINT",EDGE,{"derivedFrom":subQ0}),1.0]])]});}
            var Q53;
            {var subQ0=sQuery(id+"F0.wireOp",EDGE,"E3.67.1");var subQ1=sQuery(id+"F0.wireOp",EDGE,"E1");var subQ2=makeQuery(id+"F0.imprint","INTERSECT",VERTEX,{"derivedFrom":[subQ1,subQ0]});Q53=makeQuery(id+"F0.imprint","IMPRINT",FACE,{"disambiguationData":[TD([[makeQuery(id+"F0.imprint","IMPRINT",EDGE,{"disambiguationData":[TD([[subQ2,-1.0]])],"derivedFrom":subQ1}),-1.0]])]});}
            var Q54;
            {var subQ0=sQuery(id+"F0.wireOp",EDGE,"E3.35.1");var subQ1=sQuery(id+"F0.wireOp",EDGE,"E1");var subQ2=makeQuery(id+"F0.imprint","INTERSECT",VERTEX,{"derivedFrom":[subQ1,subQ0]});Q54=makeQuery(id+"F0.imprint","IMPRINT",FACE,{"disambiguationData":[TD([[makeQuery(id+"F0.imprint","IMPRINT",EDGE,{"disambiguationData":[TD([[subQ2,-1.0]])],"derivedFrom":subQ1}),-1.0]])]});}
            var Q55;
            {var subQ0=sQuery(id+"F0.wireOp",EDGE,"E3.48.2");var subQ1=sQuery(id+"F0.wireOp",EDGE,"E1");var subQ2=makeQuery(id+"F0.imprint","INTERSECT",VERTEX,{"derivedFrom":[subQ1,subQ0]});Q55=makeQuery(id+"F0.imprint","IMPRINT",FACE,{"disambiguationData":[TD([[makeQuery(id+"F0.imprint","IMPRINT",EDGE,{"disambiguationData":[TD([[subQ2,-1.0]])],"derivedFrom":subQ1}),-1.0]])]});}
            var Q56;
            {var subQ0=sQuery(id+"F0.wireOp",EDGE,"E3.18.0");Q56=makeQuery(id+"F0.imprint","IMPRINT",FACE,{"disambiguationData":[TD([[makeQuery(id+"F0.imprint","IMPRINT",EDGE,{"derivedFrom":subQ0}),1.0]])]});}
            var Q57;
            {var subQ0=sQuery(id+"F0.wireOp",EDGE,"E3.66.0");Q57=makeQuery(id+"F0.imprint","IMPRINT",FACE,{"disambiguationData":[TD([[makeQuery(id+"F0.imprint","IMPRINT",EDGE,{"derivedFrom":subQ0}),1.0]])]});}
            var Q58;
            {var subQ0=sQuery(id+"F0.wireOp",EDGE,"E3.34.0");Q58=makeQuery(id+"F0.imprint","IMPRINT",FACE,{"disambiguationData":[TD([[makeQuery(id+"F0.imprint","IMPRINT",EDGE,{"derivedFrom":subQ0}),1.0]])]});}
            var Q59;
            {var subQ0=sQuery(id+"F0.wireOp",EDGE,"E3.4.1");var subQ1=sQuery(id+"F0.wireOp",EDGE,"E1");var subQ2=makeQuery(id+"F0.imprint","INTERSECT",VERTEX,{"derivedFrom":[subQ1,subQ0]});Q59=makeQuery(id+"F0.imprint","IMPRINT",FACE,{"disambiguationData":[TD([[makeQuery(id+"F0.imprint","IMPRINT",EDGE,{"disambiguationData":[TD([[subQ2,-1.0]])],"derivedFrom":subQ1}),-1.0]])]});}
            var Q60;
            {var subQ0=sQuery(id+"F0.wireOp",EDGE,"E3.98.0");Q60=makeQuery(id+"F0.imprint","IMPRINT",FACE,{"disambiguationData":[TD([[makeQuery(id+"F0.imprint","IMPRINT",EDGE,{"derivedFrom":subQ0}),1.0]])]});}
            var Q61;
            {var subQ0=sQuery(id+"F0.wireOp",EDGE,"E3.68.1");var subQ1=sQuery(id+"F0.wireOp",EDGE,"E1");var subQ2=makeQuery(id+"F0.imprint","INTERSECT",VERTEX,{"derivedFrom":[subQ1,subQ0]});Q61=makeQuery(id+"F0.imprint","IMPRINT",FACE,{"disambiguationData":[TD([[makeQuery(id+"F0.imprint","IMPRINT",EDGE,{"disambiguationData":[TD([[subQ2,-1.0]])],"derivedFrom":subQ1}),-1.0]])]});}
            var Q62;
            {var subQ0=sQuery(id+"F0.wireOp",EDGE,"E3.52.1");var subQ1=sQuery(id+"F0.wireOp",EDGE,"E1");var subQ2=makeQuery(id+"F0.imprint","INTERSECT",VERTEX,{"derivedFrom":[subQ1,subQ0]});Q62=makeQuery(id+"F0.imprint","IMPRINT",FACE,{"disambiguationData":[TD([[makeQuery(id+"F0.imprint","IMPRINT",EDGE,{"disambiguationData":[TD([[subQ2,-1.0]])],"derivedFrom":subQ1}),-1.0]])]});}
            var Q63;
            {var subQ0=sQuery(id+"F0.wireOp",EDGE,"E3.36.1");var subQ1=sQuery(id+"F0.wireOp",EDGE,"E1");var subQ2=makeQuery(id+"F0.imprint","INTERSECT",VERTEX,{"derivedFrom":[subQ1,subQ0]});Q63=makeQuery(id+"F0.imprint","IMPRINT",FACE,{"disambiguationData":[TD([[makeQuery(id+"F0.imprint","IMPRINT",EDGE,{"disambiguationData":[TD([[subQ2,-1.0]])],"derivedFrom":subQ1}),-1.0]])]});}
            var Q64;
            {var subQ0=sQuery(id+"F0.wireOp",EDGE,"E3.49.2");var subQ1=sQuery(id+"F0.wireOp",EDGE,"E1");var subQ2=makeQuery(id+"F0.imprint","INTERSECT",VERTEX,{"derivedFrom":[subQ1,subQ0]});Q64=makeQuery(id+"F0.imprint","IMPRINT",FACE,{"disambiguationData":[TD([[makeQuery(id+"F0.imprint","IMPRINT",EDGE,{"disambiguationData":[TD([[subQ2,-1.0]])],"derivedFrom":subQ1}),-1.0]])]});}
            var Q65;
            {var subQ0=sQuery(id+"F0.wireOp",EDGE,"E3.17.2");var subQ1=sQuery(id+"F0.wireOp",EDGE,"E1");var subQ2=makeQuery(id+"F0.imprint","INTERSECT",VERTEX,{"derivedFrom":[subQ1,subQ0]});Q65=makeQuery(id+"F0.imprint","IMPRINT",FACE,{"disambiguationData":[TD([[makeQuery(id+"F0.imprint","IMPRINT",EDGE,{"disambiguationData":[TD([[subQ2,-1.0]])],"derivedFrom":subQ1}),-1.0]])]});}
            var Q66;
            {var subQ0=sQuery(id+"F0.wireOp",EDGE,"E3.1.2");var subQ1=sQuery(id+"F0.wireOp",EDGE,"E1");var subQ2=makeQuery(id+"F0.imprint","INTERSECT",VERTEX,{"derivedFrom":[subQ1,subQ0]});Q66=makeQuery(id+"F0.imprint","IMPRINT",FACE,{"disambiguationData":[TD([[makeQuery(id+"F0.imprint","IMPRINT",EDGE,{"disambiguationData":[TD([[subQ2,-1.0]])],"derivedFrom":subQ1}),-1.0]])]});}
            var Q67;
            {var subQ0=sQuery(id+"F0.wireOp",EDGE,"E3.83.0");Q67=makeQuery(id+"F0.imprint","IMPRINT",FACE,{"disambiguationData":[TD([[makeQuery(id+"F0.imprint","IMPRINT",EDGE,{"derivedFrom":subQ0}),1.0]])]});}
            var Q68;
            {var subQ0=sQuery(id+"F0.wireOp",EDGE,"E3.51.0");Q68=makeQuery(id+"F0.imprint","IMPRINT",FACE,{"disambiguationData":[TD([[makeQuery(id+"F0.imprint","IMPRINT",EDGE,{"derivedFrom":subQ0}),1.0]])]});}
            var Q69;
            {var subQ0=sQuery(id+"F0.wireOp",EDGE,"E3.35.0");Q69=makeQuery(id+"F0.imprint","IMPRINT",FACE,{"disambiguationData":[TD([[makeQuery(id+"F0.imprint","IMPRINT",EDGE,{"derivedFrom":subQ0}),1.0]])]});}
            var Q70;
            {var subQ0=sQuery(id+"F0.wireOp",EDGE,"E3.5.1");var subQ1=sQuery(id+"F0.wireOp",EDGE,"E1");var subQ2=makeQuery(id+"F0.imprint","INTERSECT",VERTEX,{"derivedFrom":[subQ1,subQ0]});Q70=makeQuery(id+"F0.imprint","IMPRINT",FACE,{"disambiguationData":[TD([[makeQuery(id+"F0.imprint","IMPRINT",EDGE,{"disambiguationData":[TD([[subQ2,-1.0]])],"derivedFrom":subQ1}),-1.0]])]});}
            var Q71;
            {var subQ0=sQuery(id+"F0.wireOp",EDGE,"E3.89.1");var subQ1=sQuery(id+"F0.wireOp",EDGE,"E1");var subQ2=makeQuery(id+"F0.imprint","INTERSECT",VERTEX,{"derivedFrom":[subQ1,subQ0]});Q71=makeQuery(id+"F0.imprint","IMPRINT",FACE,{"disambiguationData":[TD([[makeQuery(id+"F0.imprint","IMPRINT",EDGE,{"disambiguationData":[TD([[subQ2,-1.0]])],"derivedFrom":subQ1}),-1.0]])]});}
            var Q72;
            {var subQ0=sQuery(id+"F0.wireOp",EDGE,"E3.99.0");Q72=makeQuery(id+"F0.imprint","IMPRINT",FACE,{"disambiguationData":[TD([[makeQuery(id+"F0.imprint","IMPRINT",EDGE,{"derivedFrom":subQ0}),1.0]])]});}
            var Q73;
            {var subQ0=sQuery(id+"F0.wireOp",EDGE,"E3.69.1");var subQ1=sQuery(id+"F0.wireOp",EDGE,"E1");var subQ2=makeQuery(id+"F0.imprint","INTERSECT",VERTEX,{"derivedFrom":[subQ1,subQ0]});Q73=makeQuery(id+"F0.imprint","IMPRINT",FACE,{"disambiguationData":[TD([[makeQuery(id+"F0.imprint","IMPRINT",EDGE,{"disambiguationData":[TD([[subQ2,-1.0]])],"derivedFrom":subQ1}),-1.0]])]});}
            var Q74;
            {var subQ0=sQuery(id+"F0.wireOp",EDGE,"E3.37.1");var subQ1=sQuery(id+"F0.wireOp",EDGE,"E1");var subQ2=makeQuery(id+"F0.imprint","INTERSECT",VERTEX,{"derivedFrom":[subQ1,subQ0]});Q74=makeQuery(id+"F0.imprint","IMPRINT",FACE,{"disambiguationData":[TD([[makeQuery(id+"F0.imprint","IMPRINT",EDGE,{"disambiguationData":[TD([[subQ2,-1.0]])],"derivedFrom":subQ1}),-1.0]])]});}
            var Q75;
            {var subQ0=sQuery(id+"F0.wireOp",EDGE,"E3.2.2");var subQ1=sQuery(id+"F0.wireOp",EDGE,"E1");var subQ2=makeQuery(id+"F0.imprint","INTERSECT",VERTEX,{"derivedFrom":[subQ1,subQ0]});Q75=makeQuery(id+"F0.imprint","IMPRINT",FACE,{"disambiguationData":[TD([[makeQuery(id+"F0.imprint","IMPRINT",EDGE,{"disambiguationData":[TD([[subQ2,-1.0]])],"derivedFrom":subQ1}),-1.0]])]});}
            var Q76;
            {var subQ0=sQuery(id+"F0.wireOp",EDGE,"E3.20.0");Q76=makeQuery(id+"F0.imprint","IMPRINT",FACE,{"disambiguationData":[TD([[makeQuery(id+"F0.imprint","IMPRINT",EDGE,{"derivedFrom":subQ0}),1.0]])]});}
            var Q77;
            {var subQ0=sQuery(id+"F0.wireOp",EDGE,"E3.84.0");Q77=makeQuery(id+"F0.imprint","IMPRINT",FACE,{"disambiguationData":[TD([[makeQuery(id+"F0.imprint","IMPRINT",EDGE,{"derivedFrom":subQ0}),1.0]])]});}
            var Q78;
            {var subQ0=sQuery(id+"F0.wireOp",EDGE,"E3.52.0");Q78=makeQuery(id+"F0.imprint","IMPRINT",FACE,{"disambiguationData":[TD([[makeQuery(id+"F0.imprint","IMPRINT",EDGE,{"derivedFrom":subQ0}),1.0]])]});}
            var Q79;
            {var subQ0=sQuery(id+"F0.wireOp",EDGE,"E3.36.0");Q79=makeQuery(id+"F0.imprint","IMPRINT",FACE,{"disambiguationData":[TD([[makeQuery(id+"F0.imprint","IMPRINT",EDGE,{"derivedFrom":subQ0}),1.0]])]});}
            var Q80;
            {var subQ0=sQuery(id+"F0.wireOp",EDGE,"E3.22.1");var subQ1=sQuery(id+"F0.wireOp",EDGE,"E1");var subQ2=makeQuery(id+"F0.imprint","INTERSECT",VERTEX,{"derivedFrom":[subQ1,subQ0]});Q80=makeQuery(id+"F0.imprint","IMPRINT",FACE,{"disambiguationData":[TD([[makeQuery(id+"F0.imprint","IMPRINT",EDGE,{"disambiguationData":[TD([[subQ2,-1.0]])],"derivedFrom":subQ1}),-1.0]])]});}
            var Q81;
            {var subQ0=sQuery(id+"F0.wireOp",EDGE,"E3.70.1");var subQ1=sQuery(id+"F0.wireOp",EDGE,"E1");var subQ2=makeQuery(id+"F0.imprint","INTERSECT",VERTEX,{"derivedFrom":[subQ1,subQ0]});Q81=makeQuery(id+"F0.imprint","IMPRINT",FACE,{"disambiguationData":[TD([[makeQuery(id+"F0.imprint","IMPRINT",EDGE,{"disambiguationData":[TD([[subQ2,-1.0]])],"derivedFrom":subQ1}),-1.0]])]});}
            var Q82;
            {var subQ0=sQuery(id+"F0.wireOp",EDGE,"E3.54.1");var subQ1=sQuery(id+"F0.wireOp",EDGE,"E1");var subQ2=makeQuery(id+"F0.imprint","INTERSECT",VERTEX,{"derivedFrom":[subQ1,subQ0]});Q82=makeQuery(id+"F0.imprint","IMPRINT",FACE,{"disambiguationData":[TD([[makeQuery(id+"F0.imprint","IMPRINT",EDGE,{"disambiguationData":[TD([[subQ2,-1.0]])],"derivedFrom":subQ1}),-1.0]])]});}
            var Q83;
            {var subQ0=sQuery(id+"F0.wireOp",EDGE,"E3.38.1");var subQ1=sQuery(id+"F0.wireOp",EDGE,"E1");var subQ2=makeQuery(id+"F0.imprint","INTERSECT",VERTEX,{"derivedFrom":[subQ1,subQ0]});Q83=makeQuery(id+"F0.imprint","IMPRINT",FACE,{"disambiguationData":[TD([[makeQuery(id+"F0.imprint","IMPRINT",EDGE,{"disambiguationData":[TD([[subQ2,-1.0]])],"derivedFrom":subQ1}),-1.0]])]});}
            var Q84;
            {var subQ0=sQuery(id+"F0.wireOp",EDGE,"E3.51.2");var subQ1=sQuery(id+"F0.wireOp",EDGE,"E1");var subQ2=makeQuery(id+"F0.imprint","INTERSECT",VERTEX,{"derivedFrom":[subQ1,subQ0]});Q84=makeQuery(id+"F0.imprint","IMPRINT",FACE,{"disambiguationData":[TD([[makeQuery(id+"F0.imprint","IMPRINT",EDGE,{"disambiguationData":[TD([[subQ2,-1.0]])],"derivedFrom":subQ1}),-1.0]])]});}
            var Q85;
            {var subQ0=sQuery(id+"F0.wireOp",EDGE,"E3.21.0");Q85=makeQuery(id+"F0.imprint","IMPRINT",FACE,{"disambiguationData":[TD([[makeQuery(id+"F0.imprint","IMPRINT",EDGE,{"derivedFrom":subQ0}),1.0]])]});}
            var Q86;
            {var subQ0=sQuery(id+"F0.wireOp",EDGE,"E3.85.0");Q86=makeQuery(id+"F0.imprint","IMPRINT",FACE,{"disambiguationData":[TD([[makeQuery(id+"F0.imprint","IMPRINT",EDGE,{"derivedFrom":subQ0}),1.0]])]});}
            var Q87;
            {var subQ0=sQuery(id+"F0.wireOp",EDGE,"E3.69.0");Q87=makeQuery(id+"F0.imprint","IMPRINT",FACE,{"disambiguationData":[TD([[makeQuery(id+"F0.imprint","IMPRINT",EDGE,{"derivedFrom":subQ0}),1.0]])]});}
            var Q88;
            {var subQ0=sQuery(id+"F0.wireOp",EDGE,"E3.7.1");var subQ1=sQuery(id+"F0.wireOp",EDGE,"E1");var subQ2=makeQuery(id+"F0.imprint","INTERSECT",VERTEX,{"derivedFrom":[subQ1,subQ0]});Q88=makeQuery(id+"F0.imprint","IMPRINT",FACE,{"disambiguationData":[TD([[makeQuery(id+"F0.imprint","IMPRINT",EDGE,{"disambiguationData":[TD([[subQ2,-1.0]])],"derivedFrom":subQ1}),-1.0]])]});}
            var Q89;
            {var subQ0=sQuery(id+"F0.wireOp",EDGE,"E3.76.2");var subQ1=sQuery(id+"F0.wireOp",EDGE,"E1");var subQ2=makeQuery(id+"F0.imprint","INTERSECT",VERTEX,{"derivedFrom":[subQ1,subQ0]});Q89=makeQuery(id+"F0.imprint","IMPRINT",FACE,{"disambiguationData":[TD([[makeQuery(id+"F0.imprint","IMPRINT",EDGE,{"disambiguationData":[TD([[subQ2,1.0]])],"derivedFrom":subQ1}),-1.0]])]});}
            var Q90;
            {var subQ0=sQuery(id+"F0.wireOp",EDGE,"E3.88.2");var subQ1=sQuery(id+"F0.wireOp",EDGE,"E1");var subQ2=makeQuery(id+"F0.imprint","INTERSECT",VERTEX,{"derivedFrom":[subQ1,subQ0]});Q90=makeQuery(id+"F0.imprint","IMPRINT",FACE,{"disambiguationData":[TD([[makeQuery(id+"F0.imprint","IMPRINT",EDGE,{"disambiguationData":[TD([[subQ2,-1.0]])],"derivedFrom":subQ1}),-1.0]])]});}
            var Q91;
            {var subQ0=sQuery(id+"F0.wireOp",EDGE,"E3.71.1");var subQ1=sQuery(id+"F0.wireOp",EDGE,"E1");var subQ2=makeQuery(id+"F0.imprint","INTERSECT",VERTEX,{"derivedFrom":[subQ1,subQ0]});Q91=makeQuery(id+"F0.imprint","IMPRINT",FACE,{"disambiguationData":[TD([[makeQuery(id+"F0.imprint","IMPRINT",EDGE,{"disambiguationData":[TD([[subQ2,-1.0]])],"derivedFrom":subQ1}),-1.0]])]});}
            var Q92;
            {var subQ0=sQuery(id+"F0.wireOp",EDGE,"E3.55.1");var subQ1=sQuery(id+"F0.wireOp",EDGE,"E1");var subQ2=makeQuery(id+"F0.imprint","INTERSECT",VERTEX,{"derivedFrom":[subQ1,subQ0]});Q92=makeQuery(id+"F0.imprint","IMPRINT",FACE,{"disambiguationData":[TD([[makeQuery(id+"F0.imprint","IMPRINT",EDGE,{"disambiguationData":[TD([[subQ2,-1.0]])],"derivedFrom":subQ1}),-1.0]])]});}
            var Q93;
            {var subQ0=sQuery(id+"F0.wireOp",EDGE,"E3.36.2");var subQ1=sQuery(id+"F0.wireOp",EDGE,"E1");var subQ2=makeQuery(id+"F0.imprint","INTERSECT",VERTEX,{"derivedFrom":[subQ1,subQ0]});Q93=makeQuery(id+"F0.imprint","IMPRINT",FACE,{"disambiguationData":[TD([[makeQuery(id+"F0.imprint","IMPRINT",EDGE,{"disambiguationData":[TD([[subQ2,-1.0]])],"derivedFrom":subQ1}),-1.0]])]});}
            var Q94;
            {var subQ0=sQuery(id+"F0.wireOp",EDGE,"E3.4.2");var subQ1=sQuery(id+"F0.wireOp",EDGE,"E1");var subQ2=makeQuery(id+"F0.imprint","INTERSECT",VERTEX,{"derivedFrom":[subQ1,subQ0]});Q94=makeQuery(id+"F0.imprint","IMPRINT",FACE,{"disambiguationData":[TD([[makeQuery(id+"F0.imprint","IMPRINT",EDGE,{"disambiguationData":[TD([[subQ2,-1.0]])],"derivedFrom":subQ1}),-1.0]])]});}
            var Q95;
            {var subQ0=sQuery(id+"F0.wireOp",EDGE,"E3.92.1");var subQ1=sQuery(id+"F0.wireOp",EDGE,"E1");var subQ2=makeQuery(id+"F0.imprint","INTERSECT",VERTEX,{"derivedFrom":[subQ1,subQ0]});Q95=makeQuery(id+"F0.imprint","IMPRINT",FACE,{"disambiguationData":[TD([[makeQuery(id+"F0.imprint","IMPRINT",EDGE,{"disambiguationData":[TD([[subQ2,-1.0]])],"derivedFrom":subQ1}),-1.0]])]});}
            var Q96;
            {var subQ0=sQuery(id+"F0.wireOp",EDGE,"E3.76.1");var subQ1=sQuery(id+"F0.wireOp",EDGE,"E1");var subQ2=makeQuery(id+"F0.imprint","INTERSECT",VERTEX,{"derivedFrom":[subQ1,subQ0]});Q96=makeQuery(id+"F0.imprint","IMPRINT",FACE,{"disambiguationData":[TD([[makeQuery(id+"F0.imprint","IMPRINT",EDGE,{"disambiguationData":[TD([[subQ2,-1.0]])],"derivedFrom":subQ1}),-1.0]])]});}
            var Q97;
            {var subQ0=sQuery(id+"F0.wireOp",EDGE,"E3.86.0");Q97=makeQuery(id+"F0.imprint","IMPRINT",FACE,{"disambiguationData":[TD([[makeQuery(id+"F0.imprint","IMPRINT",EDGE,{"derivedFrom":subQ0}),1.0]])]});}
            var Q98;
            {var subQ0=sQuery(id+"F0.wireOp",EDGE,"E3.70.0");Q98=makeQuery(id+"F0.imprint","IMPRINT",FACE,{"disambiguationData":[TD([[makeQuery(id+"F0.imprint","IMPRINT",EDGE,{"derivedFrom":subQ0}),1.0]])]});}
            var Q99;
            {var subQ0=sQuery(id+"F0.wireOp",EDGE,"E3.56.1");var subQ1=sQuery(id+"F0.wireOp",EDGE,"E1");var subQ2=makeQuery(id+"F0.imprint","INTERSECT",VERTEX,{"derivedFrom":[subQ1,subQ0]});Q99=makeQuery(id+"F0.imprint","IMPRINT",FACE,{"disambiguationData":[TD([[makeQuery(id+"F0.imprint","IMPRINT",EDGE,{"disambiguationData":[TD([[subQ2,-1.0]])],"derivedFrom":subQ1}),-1.0]])]});}
            var Q100;
            {var subQ0=sQuery(id+"F0.wireOp",EDGE,"E3.40.1");var subQ1=sQuery(id+"F0.wireOp",EDGE,"E1");var subQ2=makeQuery(id+"F0.imprint","INTERSECT",VERTEX,{"derivedFrom":[subQ1,subQ0]});Q100=makeQuery(id+"F0.imprint","IMPRINT",FACE,{"disambiguationData":[TD([[makeQuery(id+"F0.imprint","IMPRINT",EDGE,{"disambiguationData":[TD([[subQ2,-1.0]])],"derivedFrom":subQ1}),-1.0]])]});}
            var Q101;
            {var subQ0=sQuery(id+"F0.wireOp",EDGE,"E3.24.1");var subQ1=sQuery(id+"F0.wireOp",EDGE,"E1");var subQ2=makeQuery(id+"F0.imprint","INTERSECT",VERTEX,{"derivedFrom":[subQ1,subQ0]});Q101=makeQuery(id+"F0.imprint","IMPRINT",FACE,{"disambiguationData":[TD([[makeQuery(id+"F0.imprint","IMPRINT",EDGE,{"disambiguationData":[TD([[subQ2,-1.0]])],"derivedFrom":subQ1}),-1.0]])]});}
            var Q102;
            {var subQ0=sQuery(id+"F0.wireOp",EDGE,"E3.8.1");var subQ1=sQuery(id+"F0.wireOp",EDGE,"E1");var subQ2=makeQuery(id+"F0.imprint","INTERSECT",VERTEX,{"derivedFrom":[subQ1,subQ0]});Q102=makeQuery(id+"F0.imprint","IMPRINT",FACE,{"disambiguationData":[TD([[makeQuery(id+"F0.imprint","IMPRINT",EDGE,{"disambiguationData":[TD([[subQ2,-1.0]])],"derivedFrom":subQ1}),-1.0]])]});}
            var Q103;
            {var subQ0=sQuery(id+"F0.wireOp",EDGE,"E3.21.2");var subQ1=sQuery(id+"F0.wireOp",EDGE,"E1");var subQ2=makeQuery(id+"F0.imprint","INTERSECT",VERTEX,{"derivedFrom":[subQ1,subQ0]});Q103=makeQuery(id+"F0.imprint","IMPRINT",FACE,{"disambiguationData":[TD([[makeQuery(id+"F0.imprint","IMPRINT",EDGE,{"disambiguationData":[TD([[subQ2,-1.0]])],"derivedFrom":subQ1}),-1.0]])]});}
            var Q104;
            {var subQ0=sQuery(id+"F0.wireOp",EDGE,"E3.5.2");var subQ1=sQuery(id+"F0.wireOp",EDGE,"E1");var subQ2=makeQuery(id+"F0.imprint","INTERSECT",VERTEX,{"derivedFrom":[subQ1,subQ0]});Q104=makeQuery(id+"F0.imprint","IMPRINT",FACE,{"disambiguationData":[TD([[makeQuery(id+"F0.imprint","IMPRINT",EDGE,{"disambiguationData":[TD([[subQ2,-1.0]])],"derivedFrom":subQ1}),-1.0]])]});}
            var Q105;
            {var subQ0=sQuery(id+"F0.wireOp",EDGE,"E3.53.2");var subQ1=sQuery(id+"F0.wireOp",EDGE,"E1");var subQ2=makeQuery(id+"F0.imprint","INTERSECT",VERTEX,{"derivedFrom":[subQ1,subQ0]});Q105=makeQuery(id+"F0.imprint","IMPRINT",FACE,{"disambiguationData":[TD([[makeQuery(id+"F0.imprint","IMPRINT",EDGE,{"disambiguationData":[TD([[subQ2,-1.0]])],"derivedFrom":subQ1}),-1.0]])]});}
            var Q106;
            {var subQ0=sQuery(id+"F0.wireOp",EDGE,"E3.54.0");Q106=makeQuery(id+"F0.imprint","IMPRINT",FACE,{"disambiguationData":[TD([[makeQuery(id+"F0.imprint","IMPRINT",EDGE,{"derivedFrom":subQ0}),1.0]])]});}
            var Q107;
            {var subQ0=sQuery(id+"F0.wireOp",EDGE,"E3.22.0");Q107=makeQuery(id+"F0.imprint","IMPRINT",FACE,{"disambiguationData":[TD([[makeQuery(id+"F0.imprint","IMPRINT",EDGE,{"derivedFrom":subQ0}),1.0]])]});}
            var Q108;
            {var subQ0=sQuery(id+"F0.wireOp",EDGE,"E3.57.1");var subQ1=sQuery(id+"F0.wireOp",EDGE,"E1");var subQ2=makeQuery(id+"F0.imprint","INTERSECT",VERTEX,{"derivedFrom":[subQ1,subQ0]});Q108=makeQuery(id+"F0.imprint","IMPRINT",FACE,{"disambiguationData":[TD([[makeQuery(id+"F0.imprint","IMPRINT",EDGE,{"disambiguationData":[TD([[subQ2,-1.0]])],"derivedFrom":subQ1}),-1.0]])]});}
            var Q109;
            {var subQ0=sQuery(id+"F0.wireOp",EDGE,"E3.41.1");var subQ1=sQuery(id+"F0.wireOp",EDGE,"E1");var subQ2=makeQuery(id+"F0.imprint","INTERSECT",VERTEX,{"derivedFrom":[subQ1,subQ0]});Q109=makeQuery(id+"F0.imprint","IMPRINT",FACE,{"disambiguationData":[TD([[makeQuery(id+"F0.imprint","IMPRINT",EDGE,{"disambiguationData":[TD([[subQ2,-1.0]])],"derivedFrom":subQ1}),-1.0]])]});}
            var Q110;
            {var subQ0=sQuery(id+"F0.wireOp",EDGE,"E3.25.1");var subQ1=sQuery(id+"F0.wireOp",EDGE,"E1");var subQ2=makeQuery(id+"F0.imprint","INTERSECT",VERTEX,{"derivedFrom":[subQ1,subQ0]});Q110=makeQuery(id+"F0.imprint","IMPRINT",FACE,{"disambiguationData":[TD([[makeQuery(id+"F0.imprint","IMPRINT",EDGE,{"disambiguationData":[TD([[subQ2,-1.0]])],"derivedFrom":subQ1}),-1.0]])]});}
            var Q111;
            {var subQ0=sQuery(id+"F0.wireOp",EDGE,"E3.22.2");var subQ1=sQuery(id+"F0.wireOp",EDGE,"E1");var subQ2=makeQuery(id+"F0.imprint","INTERSECT",VERTEX,{"derivedFrom":[subQ1,subQ0]});Q111=makeQuery(id+"F0.imprint","IMPRINT",FACE,{"disambiguationData":[TD([[makeQuery(id+"F0.imprint","IMPRINT",EDGE,{"disambiguationData":[TD([[subQ2,-1.0]])],"derivedFrom":subQ1}),-1.0]])]});}
            var Q112;
            {var subQ0=sQuery(id+"F0.wireOp",EDGE,"E3.54.2");var subQ1=sQuery(id+"F0.wireOp",EDGE,"E1");var subQ2=makeQuery(id+"F0.imprint","INTERSECT",VERTEX,{"derivedFrom":[subQ1,subQ0]});Q112=makeQuery(id+"F0.imprint","IMPRINT",FACE,{"disambiguationData":[TD([[makeQuery(id+"F0.imprint","IMPRINT",EDGE,{"disambiguationData":[TD([[subQ2,-1.0]])],"derivedFrom":subQ1}),-1.0]])]});}
            var Q113;
            {var subQ0=sQuery(id+"F0.wireOp",EDGE,"E3.55.0");Q113=makeQuery(id+"F0.imprint","IMPRINT",FACE,{"disambiguationData":[TD([[makeQuery(id+"F0.imprint","IMPRINT",EDGE,{"derivedFrom":subQ0}),1.0]])]});}
            var Q114;
            {var subQ0=sQuery(id+"F0.wireOp",EDGE,"E3.39.0");Q114=makeQuery(id+"F0.imprint","IMPRINT",FACE,{"disambiguationData":[TD([[makeQuery(id+"F0.imprint","IMPRINT",EDGE,{"derivedFrom":subQ0}),1.0]])]});}
            var Q115;
            {var subQ0=sQuery(id+"F0.wireOp",EDGE,"E3.23.0");Q115=makeQuery(id+"F0.imprint","IMPRINT",FACE,{"disambiguationData":[TD([[makeQuery(id+"F0.imprint","IMPRINT",EDGE,{"derivedFrom":subQ0}),1.0]])]});}
            var Q116;
            {var subQ0=sQuery(id+"F0.wireOp",EDGE,"E3.87.0");Q116=makeQuery(id+"F0.imprint","IMPRINT",FACE,{"disambiguationData":[TD([[makeQuery(id+"F0.imprint","IMPRINT",EDGE,{"derivedFrom":subQ0}),1.0]])]});}
            var Q117;
            {var subQ0=sQuery(id+"F0.wireOp",EDGE,"E3.74.1");var subQ1=sQuery(id+"F0.wireOp",EDGE,"E1");var subQ2=makeQuery(id+"F0.imprint","INTERSECT",VERTEX,{"derivedFrom":[subQ1,subQ0]});Q117=makeQuery(id+"F0.imprint","IMPRINT",FACE,{"disambiguationData":[TD([[makeQuery(id+"F0.imprint","IMPRINT",EDGE,{"disambiguationData":[TD([[subQ2,-1.0]])],"derivedFrom":subQ1}),-1.0]])]});}
            var Q118;
            {var subQ0=sQuery(id+"F0.wireOp",EDGE,"E3.71.2");var subQ1=sQuery(id+"F0.wireOp",EDGE,"E1");var subQ2=makeQuery(id+"F0.imprint","INTERSECT",VERTEX,{"derivedFrom":[subQ1,subQ0]});Q118=makeQuery(id+"F0.imprint","IMPRINT",FACE,{"disambiguationData":[TD([[makeQuery(id+"F0.imprint","IMPRINT",EDGE,{"disambiguationData":[TD([[subQ2,-1.0]])],"derivedFrom":subQ1}),-1.0]])]});}
            var Q119;
            {var subQ0=sQuery(id+"F0.wireOp",EDGE,"E3.39.2");var subQ1=sQuery(id+"F0.wireOp",EDGE,"E1");var subQ2=makeQuery(id+"F0.imprint","INTERSECT",VERTEX,{"derivedFrom":[subQ1,subQ0]});Q119=makeQuery(id+"F0.imprint","IMPRINT",FACE,{"disambiguationData":[TD([[makeQuery(id+"F0.imprint","IMPRINT",EDGE,{"disambiguationData":[TD([[subQ2,-1.0]])],"derivedFrom":subQ1}),-1.0]])]});}
            var Q120;
            {var subQ0=sQuery(id+"F0.wireOp",EDGE,"E3.40.0");Q120=makeQuery(id+"F0.imprint","IMPRINT",FACE,{"disambiguationData":[TD([[makeQuery(id+"F0.imprint","IMPRINT",EDGE,{"derivedFrom":subQ0}),1.0]])]});}
            var Q121;
            {var subQ0=sQuery(id+"F0.wireOp",EDGE,"E3.24.0");Q121=makeQuery(id+"F0.imprint","IMPRINT",FACE,{"disambiguationData":[TD([[makeQuery(id+"F0.imprint","IMPRINT",EDGE,{"derivedFrom":subQ0}),1.0]])]});}
            var Q122;
            {var subQ0=sQuery(id+"F0.wireOp",EDGE,"E3.94.1");var subQ1=sQuery(id+"F0.wireOp",EDGE,"E1");var subQ2=makeQuery(id+"F0.imprint","INTERSECT",VERTEX,{"derivedFrom":[subQ1,subQ0]});Q122=makeQuery(id+"F0.imprint","IMPRINT",FACE,{"disambiguationData":[TD([[makeQuery(id+"F0.imprint","IMPRINT",EDGE,{"disambiguationData":[TD([[subQ2,-1.0]])],"derivedFrom":subQ1}),-1.0]])]});}
            var Q123;
            {var subQ0=sQuery(id+"F0.wireOp",EDGE,"E3.72.0");Q123=makeQuery(id+"F0.imprint","IMPRINT",FACE,{"disambiguationData":[TD([[makeQuery(id+"F0.imprint","IMPRINT",EDGE,{"derivedFrom":subQ0}),1.0]])]});}
            var Q124;
            {var subQ0=sQuery(id+"F0.wireOp",EDGE,"E3.58.1");var subQ1=sQuery(id+"F0.wireOp",EDGE,"E1");var subQ2=makeQuery(id+"F0.imprint","INTERSECT",VERTEX,{"derivedFrom":[subQ1,subQ0]});Q124=makeQuery(id+"F0.imprint","IMPRINT",FACE,{"disambiguationData":[TD([[makeQuery(id+"F0.imprint","IMPRINT",EDGE,{"disambiguationData":[TD([[subQ2,-1.0]])],"derivedFrom":subQ1}),-1.0]])]});}
            var Q125;
            {var subQ0=sQuery(id+"F0.wireOp",EDGE,"E3.42.1");var subQ1=sQuery(id+"F0.wireOp",EDGE,"E1");var subQ2=makeQuery(id+"F0.imprint","INTERSECT",VERTEX,{"derivedFrom":[subQ1,subQ0]});Q125=makeQuery(id+"F0.imprint","IMPRINT",FACE,{"disambiguationData":[TD([[makeQuery(id+"F0.imprint","IMPRINT",EDGE,{"disambiguationData":[TD([[subQ2,-1.0]])],"derivedFrom":subQ1}),-1.0]])]});}
            var Q126;
            {var subQ0=sQuery(id+"F0.wireOp",EDGE,"E3.56.2");var subQ1=sQuery(id+"F0.wireOp",EDGE,"E1");var subQ2=makeQuery(id+"F0.imprint","INTERSECT",VERTEX,{"derivedFrom":[subQ1,subQ0]});Q126=makeQuery(id+"F0.imprint","IMPRINT",FACE,{"disambiguationData":[TD([[makeQuery(id+"F0.imprint","IMPRINT",EDGE,{"disambiguationData":[TD([[subQ2,-1.0]])],"derivedFrom":subQ1}),-1.0]])]});}
            var Q127;
            {var subQ0=sQuery(id+"F0.wireOp",EDGE,"E3.57.0");Q127=makeQuery(id+"F0.imprint","IMPRINT",FACE,{"disambiguationData":[TD([[makeQuery(id+"F0.imprint","IMPRINT",EDGE,{"derivedFrom":subQ0}),1.0]])]});}
            var Q128;
            {var subQ0=sQuery(id+"F0.wireOp",EDGE,"E3.41.0");Q128=makeQuery(id+"F0.imprint","IMPRINT",FACE,{"disambiguationData":[TD([[makeQuery(id+"F0.imprint","IMPRINT",EDGE,{"derivedFrom":subQ0}),1.0]])]});}
            var Q129;
            {var subQ0=sQuery(id+"F0.wireOp",EDGE,"E3.95.1");var subQ1=sQuery(id+"F0.wireOp",EDGE,"E1");var subQ2=makeQuery(id+"F0.imprint","INTERSECT",VERTEX,{"derivedFrom":[subQ1,subQ0]});Q129=makeQuery(id+"F0.imprint","IMPRINT",FACE,{"disambiguationData":[TD([[makeQuery(id+"F0.imprint","IMPRINT",EDGE,{"disambiguationData":[TD([[subQ2,-1.0]])],"derivedFrom":subQ1}),-1.0]])]});}
            var Q130;
            {var subQ0=sQuery(id+"F0.wireOp",EDGE,"E3.79.1");var subQ1=sQuery(id+"F0.wireOp",EDGE,"E1");var subQ2=makeQuery(id+"F0.imprint","INTERSECT",VERTEX,{"derivedFrom":[subQ1,subQ0]});Q130=makeQuery(id+"F0.imprint","IMPRINT",FACE,{"disambiguationData":[TD([[makeQuery(id+"F0.imprint","IMPRINT",EDGE,{"disambiguationData":[TD([[subQ2,-1.0]])],"derivedFrom":subQ1}),-1.0]])]});}
            var Q131;
            {var subQ0=sQuery(id+"F0.wireOp",EDGE,"E3.43.1");var subQ1=sQuery(id+"F0.wireOp",EDGE,"E1");var subQ2=makeQuery(id+"F0.imprint","INTERSECT",VERTEX,{"derivedFrom":[subQ1,subQ0]});Q131=makeQuery(id+"F0.imprint","IMPRINT",FACE,{"disambiguationData":[TD([[makeQuery(id+"F0.imprint","IMPRINT",EDGE,{"disambiguationData":[TD([[subQ2,-1.0]])],"derivedFrom":subQ1}),-1.0]])]});}
            var Q132;
            {var subQ0=sQuery(id+"F0.wireOp",EDGE,"E3.27.1");var subQ1=sQuery(id+"F0.wireOp",EDGE,"E1");var subQ2=makeQuery(id+"F0.imprint","INTERSECT",VERTEX,{"derivedFrom":[subQ1,subQ0]});Q132=makeQuery(id+"F0.imprint","IMPRINT",FACE,{"disambiguationData":[TD([[makeQuery(id+"F0.imprint","IMPRINT",EDGE,{"disambiguationData":[TD([[subQ2,-1.0]])],"derivedFrom":subQ1}),-1.0]])]});}
            var Q133;
            {var subQ0=sQuery(id+"F0.wireOp",EDGE,"E3.24.2");var subQ1=sQuery(id+"F0.wireOp",EDGE,"E1");var subQ2=makeQuery(id+"F0.imprint","INTERSECT",VERTEX,{"derivedFrom":[subQ1,subQ0]});Q133=makeQuery(id+"F0.imprint","IMPRINT",FACE,{"disambiguationData":[TD([[makeQuery(id+"F0.imprint","IMPRINT",EDGE,{"disambiguationData":[TD([[subQ2,-1.0]])],"derivedFrom":subQ1}),-1.0]])]});}
            var Q134;
            {var subQ0=sQuery(id+"F0.wireOp",EDGE,"E3.92.2");var subQ1=sQuery(id+"F0.wireOp",EDGE,"E1");var subQ2=makeQuery(id+"F0.imprint","INTERSECT",VERTEX,{"derivedFrom":[subQ1,subQ0]});Q134=makeQuery(id+"F0.imprint","IMPRINT",FACE,{"disambiguationData":[TD([[makeQuery(id+"F0.imprint","IMPRINT",EDGE,{"disambiguationData":[TD([[subQ2,-1.0]])],"derivedFrom":subQ1}),-1.0]])]});}
            var Q135;
            {var subQ0=sQuery(id+"F0.wireOp",EDGE,"E3.76.2");var subQ1=sQuery(id+"F0.wireOp",EDGE,"E1");var subQ2=makeQuery(id+"F0.imprint","INTERSECT",VERTEX,{"derivedFrom":[subQ1,subQ0]});Q135=makeQuery(id+"F0.imprint","IMPRINT",FACE,{"disambiguationData":[TD([[makeQuery(id+"F0.imprint","IMPRINT",EDGE,{"disambiguationData":[TD([[subQ2,-1.0]])],"derivedFrom":subQ1}),-1.0]])]});}
            var Q136;
            {var subQ0=sQuery(id+"F0.wireOp",EDGE,"E3.58.0");Q136=makeQuery(id+"F0.imprint","IMPRINT",FACE,{"disambiguationData":[TD([[makeQuery(id+"F0.imprint","IMPRINT",EDGE,{"derivedFrom":subQ0}),1.0]])]});}
            var Q137;
            {var subQ0=sQuery(id+"F0.wireOp",EDGE,"E3.26.0");Q137=makeQuery(id+"F0.imprint","IMPRINT",FACE,{"disambiguationData":[TD([[makeQuery(id+"F0.imprint","IMPRINT",EDGE,{"derivedFrom":subQ0}),1.0]])]});}
            var Q138;
            {var subQ0=sQuery(id+"F0.wireOp",EDGE,"E3.96.1");var subQ1=sQuery(id+"F0.wireOp",EDGE,"E1");var subQ2=makeQuery(id+"F0.imprint","INTERSECT",VERTEX,{"derivedFrom":[subQ1,subQ0]});Q138=makeQuery(id+"F0.imprint","IMPRINT",FACE,{"disambiguationData":[TD([[makeQuery(id+"F0.imprint","IMPRINT",EDGE,{"disambiguationData":[TD([[subQ2,-1.0]])],"derivedFrom":subQ1}),-1.0]])]});}
            var Q139;
            {var subQ0=sQuery(id+"F0.wireOp",EDGE,"E3.80.1");var subQ1=sQuery(id+"F0.wireOp",EDGE,"E1");var subQ2=makeQuery(id+"F0.imprint","INTERSECT",VERTEX,{"derivedFrom":[subQ1,subQ0]});Q139=makeQuery(id+"F0.imprint","IMPRINT",FACE,{"disambiguationData":[TD([[makeQuery(id+"F0.imprint","IMPRINT",EDGE,{"disambiguationData":[TD([[subQ2,-1.0]])],"derivedFrom":subQ1}),-1.0]])]});}
            var Q140;
            {var subQ0=sQuery(id+"F0.wireOp",EDGE,"E3.90.0");Q140=makeQuery(id+"F0.imprint","IMPRINT",FACE,{"disambiguationData":[TD([[makeQuery(id+"F0.imprint","IMPRINT",EDGE,{"derivedFrom":subQ0}),1.0]])]});}
            var Q141;
            {var subQ0=sQuery(id+"F0.wireOp",EDGE,"E3.74.0");Q141=makeQuery(id+"F0.imprint","IMPRINT",FACE,{"disambiguationData":[TD([[makeQuery(id+"F0.imprint","IMPRINT",EDGE,{"derivedFrom":subQ0}),1.0]])]});}
            var Q142;
            {var subQ0=sQuery(id+"F0.wireOp",EDGE,"E3.60.1");var subQ1=sQuery(id+"F0.wireOp",EDGE,"E1");var subQ2=makeQuery(id+"F0.imprint","INTERSECT",VERTEX,{"derivedFrom":[subQ1,subQ0]});Q142=makeQuery(id+"F0.imprint","IMPRINT",FACE,{"disambiguationData":[TD([[makeQuery(id+"F0.imprint","IMPRINT",EDGE,{"disambiguationData":[TD([[subQ2,-1.0]])],"derivedFrom":subQ1}),-1.0]])]});}
            var Q143;
            {var subQ0=sQuery(id+"F0.wireOp",EDGE,"E3.12.1");var subQ1=sQuery(id+"F0.wireOp",EDGE,"E1");var subQ2=makeQuery(id+"F0.imprint","INTERSECT",VERTEX,{"derivedFrom":[subQ1,subQ0]});Q143=makeQuery(id+"F0.imprint","IMPRINT",FACE,{"disambiguationData":[TD([[makeQuery(id+"F0.imprint","IMPRINT",EDGE,{"disambiguationData":[TD([[subQ2,-1.0]])],"derivedFrom":subQ1}),-1.0]])]});}
            var Q144;
            {var subQ0=sQuery(id+"F0.wireOp",EDGE,"E3.93.2");var subQ1=sQuery(id+"F0.wireOp",EDGE,"E1");var subQ2=makeQuery(id+"F0.imprint","INTERSECT",VERTEX,{"derivedFrom":[subQ1,subQ0]});Q144=makeQuery(id+"F0.imprint","IMPRINT",FACE,{"disambiguationData":[TD([[makeQuery(id+"F0.imprint","IMPRINT",EDGE,{"disambiguationData":[TD([[subQ2,-1.0]])],"derivedFrom":subQ1}),-1.0]])]});}
            var Q145;
            {var subQ0=sQuery(id+"F0.wireOp",EDGE,"E3.73.2");var subQ1=sQuery(id+"F0.wireOp",EDGE,"E1");var subQ2=makeQuery(id+"F0.imprint","INTERSECT",VERTEX,{"derivedFrom":[subQ1,subQ0]});Q145=makeQuery(id+"F0.imprint","IMPRINT",FACE,{"disambiguationData":[TD([[makeQuery(id+"F0.imprint","IMPRINT",EDGE,{"disambiguationData":[TD([[subQ2,-1.0]])],"derivedFrom":subQ1}),-1.0]])]});}
            var Q146;
            {var subQ0=sQuery(id+"F0.wireOp",EDGE,"E3.59.0");Q146=makeQuery(id+"F0.imprint","IMPRINT",FACE,{"disambiguationData":[TD([[makeQuery(id+"F0.imprint","IMPRINT",EDGE,{"derivedFrom":subQ0}),1.0]])]});}
            var Q147;
            {var subQ0=sQuery(id+"F0.wireOp",EDGE,"E3.97.1");var subQ1=sQuery(id+"F0.wireOp",EDGE,"E1");var subQ2=makeQuery(id+"F0.imprint","INTERSECT",VERTEX,{"derivedFrom":[subQ1,subQ0]});Q147=makeQuery(id+"F0.imprint","IMPRINT",FACE,{"disambiguationData":[TD([[makeQuery(id+"F0.imprint","IMPRINT",EDGE,{"disambiguationData":[TD([[subQ2,-1.0]])],"derivedFrom":subQ1}),-1.0]])]});}
            var Q148;
            {var subQ0=sQuery(id+"F0.wireOp",EDGE,"E3.81.1");var subQ1=sQuery(id+"F0.wireOp",EDGE,"E1");var subQ2=makeQuery(id+"F0.imprint","INTERSECT",VERTEX,{"derivedFrom":[subQ1,subQ0]});Q148=makeQuery(id+"F0.imprint","IMPRINT",FACE,{"disambiguationData":[TD([[makeQuery(id+"F0.imprint","IMPRINT",EDGE,{"disambiguationData":[TD([[subQ2,-1.0]])],"derivedFrom":subQ1}),-1.0]])]});}
            var Q149;
            {var subQ0=sQuery(id+"F0.wireOp",EDGE,"E3.91.0");Q149=makeQuery(id+"F0.imprint","IMPRINT",FACE,{"disambiguationData":[TD([[makeQuery(id+"F0.imprint","IMPRINT",EDGE,{"derivedFrom":subQ0}),1.0]])]});}
            var Q150;
            {var subQ0=sQuery(id+"F0.wireOp",EDGE,"E3.61.1");var subQ1=sQuery(id+"F0.wireOp",EDGE,"E1");var subQ2=makeQuery(id+"F0.imprint","INTERSECT",VERTEX,{"derivedFrom":[subQ1,subQ0]});Q150=makeQuery(id+"F0.imprint","IMPRINT",FACE,{"disambiguationData":[TD([[makeQuery(id+"F0.imprint","IMPRINT",EDGE,{"disambiguationData":[TD([[subQ2,-1.0]])],"derivedFrom":subQ1}),-1.0]])]});}
            var Q151;
            {var subQ0=sQuery(id+"F0.wireOp",EDGE,"E3.13.1");var subQ1=sQuery(id+"F0.wireOp",EDGE,"E1");var subQ2=makeQuery(id+"F0.imprint","INTERSECT",VERTEX,{"derivedFrom":[subQ1,subQ0]});Q151=makeQuery(id+"F0.imprint","IMPRINT",FACE,{"disambiguationData":[TD([[makeQuery(id+"F0.imprint","IMPRINT",EDGE,{"disambiguationData":[TD([[subQ2,-1.0]])],"derivedFrom":subQ1}),-1.0]])]});}
            var Q152;
            {var subQ0=sQuery(id+"F0.wireOp",EDGE,"E3.26.2");var subQ1=sQuery(id+"F0.wireOp",EDGE,"E1");var subQ2=makeQuery(id+"F0.imprint","INTERSECT",VERTEX,{"derivedFrom":[subQ1,subQ0]});Q152=makeQuery(id+"F0.imprint","IMPRINT",FACE,{"disambiguationData":[TD([[makeQuery(id+"F0.imprint","IMPRINT",EDGE,{"disambiguationData":[TD([[subQ2,-1.0]])],"derivedFrom":subQ1}),-1.0]])]});}
            var Q153;
            {var subQ0=sQuery(id+"F0.wireOp",EDGE,"E3.78.2");var subQ1=sQuery(id+"F0.wireOp",EDGE,"E1");var subQ2=makeQuery(id+"F0.imprint","INTERSECT",VERTEX,{"derivedFrom":[subQ1,subQ0]});Q153=makeQuery(id+"F0.imprint","IMPRINT",FACE,{"disambiguationData":[TD([[makeQuery(id+"F0.imprint","IMPRINT",EDGE,{"disambiguationData":[TD([[subQ2,-1.0]])],"derivedFrom":subQ1}),-1.0]])]});}
            var Q154;
            {var subQ0=sQuery(id+"F0.wireOp",EDGE,"E3.74.2");var subQ1=sQuery(id+"F0.wireOp",EDGE,"E1");var subQ2=makeQuery(id+"F0.imprint","INTERSECT",VERTEX,{"derivedFrom":[subQ1,subQ0]});Q154=makeQuery(id+"F0.imprint","IMPRINT",FACE,{"disambiguationData":[TD([[makeQuery(id+"F0.imprint","IMPRINT",EDGE,{"disambiguationData":[TD([[subQ2,-1.0]])],"derivedFrom":subQ1}),-1.0]])]});}
            var Q155;
            {var subQ0=sQuery(id+"F0.wireOp",EDGE,"E3.58.2");var subQ1=sQuery(id+"F0.wireOp",EDGE,"E1");var subQ2=makeQuery(id+"F0.imprint","INTERSECT",VERTEX,{"derivedFrom":[subQ1,subQ0]});Q155=makeQuery(id+"F0.imprint","IMPRINT",FACE,{"disambiguationData":[TD([[makeQuery(id+"F0.imprint","IMPRINT",EDGE,{"disambiguationData":[TD([[subQ2,-1.0]])],"derivedFrom":subQ1}),-1.0]])]});}
            var Q156;
            {var subQ0=sQuery(id+"F0.wireOp",EDGE,"E3.60.0");Q156=makeQuery(id+"F0.imprint","IMPRINT",FACE,{"disambiguationData":[TD([[makeQuery(id+"F0.imprint","IMPRINT",EDGE,{"derivedFrom":subQ0}),1.0]])]});}
            var Q157;
            {var subQ0=sQuery(id+"F0.wireOp",EDGE,"E3.44.0");Q157=makeQuery(id+"F0.imprint","IMPRINT",FACE,{"disambiguationData":[TD([[makeQuery(id+"F0.imprint","IMPRINT",EDGE,{"derivedFrom":subQ0}),1.0]])]});}
            var Q158;
            {var subQ0=sQuery(id+"F0.wireOp",EDGE,"E3.28.0");Q158=makeQuery(id+"F0.imprint","IMPRINT",FACE,{"disambiguationData":[TD([[makeQuery(id+"F0.imprint","IMPRINT",EDGE,{"derivedFrom":subQ0}),1.0]])]});}
            var Q159;
            {var subQ0=sQuery(id+"F0.wireOp",EDGE,"E3.98.1");var subQ1=sQuery(id+"F0.wireOp",EDGE,"E1");var subQ2=makeQuery(id+"F0.imprint","INTERSECT",VERTEX,{"derivedFrom":[subQ1,subQ0]});Q159=makeQuery(id+"F0.imprint","IMPRINT",FACE,{"disambiguationData":[TD([[makeQuery(id+"F0.imprint","IMPRINT",EDGE,{"disambiguationData":[TD([[subQ2,-1.0]])],"derivedFrom":subQ1}),-1.0]])]});}
            var Q160;
            {var subQ0=sQuery(id+"F0.wireOp",EDGE,"E3.82.1");var subQ1=sQuery(id+"F0.wireOp",EDGE,"E1");var subQ2=makeQuery(id+"F0.imprint","INTERSECT",VERTEX,{"derivedFrom":[subQ1,subQ0]});Q160=makeQuery(id+"F0.imprint","IMPRINT",FACE,{"disambiguationData":[TD([[makeQuery(id+"F0.imprint","IMPRINT",EDGE,{"disambiguationData":[TD([[subQ2,-1.0]])],"derivedFrom":subQ1}),-1.0]])]});}
            var Q161;
            {var subQ0=sQuery(id+"F0.wireOp",EDGE,"E3.92.0");Q161=makeQuery(id+"F0.imprint","IMPRINT",FACE,{"disambiguationData":[TD([[makeQuery(id+"F0.imprint","IMPRINT",EDGE,{"derivedFrom":subQ0}),1.0]])]});}
            var Q162;
            {var subQ0=sQuery(id+"F0.wireOp",EDGE,"E3.76.0");Q162=makeQuery(id+"F0.imprint","IMPRINT",FACE,{"disambiguationData":[TD([[makeQuery(id+"F0.imprint","IMPRINT",EDGE,{"derivedFrom":subQ0}),1.0]])]});}
            var Q163;
            {var subQ0=sQuery(id+"F0.wireOp",EDGE,"E3.62.1");var subQ1=sQuery(id+"F0.wireOp",EDGE,"E1");var subQ2=makeQuery(id+"F0.imprint","INTERSECT",VERTEX,{"derivedFrom":[subQ1,subQ0]});Q163=makeQuery(id+"F0.imprint","IMPRINT",FACE,{"disambiguationData":[TD([[makeQuery(id+"F0.imprint","IMPRINT",EDGE,{"disambiguationData":[TD([[subQ2,-1.0]])],"derivedFrom":subQ1}),-1.0]])]});}
            var Q164;
            {var subQ0=sQuery(id+"F0.wireOp",EDGE,"E3.14.1");var subQ1=sQuery(id+"F0.wireOp",EDGE,"E1");var subQ2=makeQuery(id+"F0.imprint","INTERSECT",VERTEX,{"derivedFrom":[subQ1,subQ0]});Q164=makeQuery(id+"F0.imprint","IMPRINT",FACE,{"disambiguationData":[TD([[makeQuery(id+"F0.imprint","IMPRINT",EDGE,{"disambiguationData":[TD([[subQ2,-1.0]])],"derivedFrom":subQ1}),-1.0]])]});}
            var Q165;
            {var subQ0=sQuery(id+"F0.wireOp",EDGE,"E3.27.2");var subQ1=sQuery(id+"F0.wireOp",EDGE,"E1");var subQ2=makeQuery(id+"F0.imprint","INTERSECT",VERTEX,{"derivedFrom":[subQ1,subQ0]});Q165=makeQuery(id+"F0.imprint","IMPRINT",FACE,{"disambiguationData":[TD([[makeQuery(id+"F0.imprint","IMPRINT",EDGE,{"disambiguationData":[TD([[subQ2,-1.0]])],"derivedFrom":subQ1}),-1.0]])]});}
            var Q166;
            {var subQ0=sQuery(id+"F0.wireOp",EDGE,"E3.15.0");Q166=makeQuery(id+"F0.imprint","IMPRINT",FACE,{"disambiguationData":[TD([[makeQuery(id+"F0.imprint","IMPRINT",EDGE,{"derivedFrom":subQ0}),1.0]])]});}
            var Q167;
            {var subQ0=sQuery(id+"F0.wireOp",EDGE,"E3.13.0");Q167=makeQuery(id+"F0.imprint","IMPRINT",FACE,{"disambiguationData":[TD([[makeQuery(id+"F0.imprint","IMPRINT",EDGE,{"derivedFrom":subQ0}),1.0]])]});}
            var Q168;
            {var subQ0=sQuery(id+"F0.wireOp",EDGE,"E3.14.0");Q168=makeQuery(id+"F0.imprint","IMPRINT",FACE,{"disambiguationData":[TD([[makeQuery(id+"F0.imprint","IMPRINT",EDGE,{"derivedFrom":subQ0}),1.0]])]});}
            var Q169;
            {var subQ0=sQuery(id+"F0.wireOp",EDGE,"E3.1.0");Q169=makeQuery(id+"F0.imprint","IMPRINT",FACE,{"disambiguationData":[TD([[makeQuery(id+"F0.imprint","IMPRINT",EDGE,{"derivedFrom":subQ0}),1.0]])]});}
            var Q170;
            {var subQ0=sQuery(id+"F0.wireOp",EDGE,"E3.3.0");Q170=makeQuery(id+"F0.imprint","IMPRINT",FACE,{"disambiguationData":[TD([[makeQuery(id+"F0.imprint","IMPRINT",EDGE,{"derivedFrom":subQ0}),1.0]])]});}
            var Q171;
            {var subQ0=sQuery(id+"F0.wireOp",EDGE,"E3.5.0");Q171=makeQuery(id+"F0.imprint","IMPRINT",FACE,{"disambiguationData":[TD([[makeQuery(id+"F0.imprint","IMPRINT",EDGE,{"derivedFrom":subQ0}),1.0]])]});}
            var Q172;
            {var subQ0=sQuery(id+"F0.wireOp",EDGE,"E3.6.0");Q172=makeQuery(id+"F0.imprint","IMPRINT",FACE,{"disambiguationData":[TD([[makeQuery(id+"F0.imprint","IMPRINT",EDGE,{"derivedFrom":subQ0}),1.0]])]});}
            var Q173;
            {var subQ0=sQuery(id+"F0.wireOp",EDGE,"E3.9.0");Q173=makeQuery(id+"F0.imprint","IMPRINT",FACE,{"disambiguationData":[TD([[makeQuery(id+"F0.imprint","IMPRINT",EDGE,{"derivedFrom":subQ0}),1.0]])]});}
            var Q174;
            {var subQ0=sQuery(id+"F0.wireOp",EDGE,"E3.10.0");Q174=makeQuery(id+"F0.imprint","IMPRINT",FACE,{"disambiguationData":[TD([[makeQuery(id+"F0.imprint","IMPRINT",EDGE,{"derivedFrom":subQ0}),1.0]])]});}
            var Q175;
            {var subQ0=sQuery(id+"F0.wireOp",EDGE,"E3.11.0");Q175=makeQuery(id+"F0.imprint","IMPRINT",FACE,{"disambiguationData":[TD([[makeQuery(id+"F0.imprint","IMPRINT",EDGE,{"derivedFrom":subQ0}),1.0]])]});}
            var Q176;
            {var subQ0=sQuery(id+"F0.wireOp",EDGE,"E3.12.0");Q176=makeQuery(id+"F0.imprint","IMPRINT",FACE,{"disambiguationData":[TD([[makeQuery(id+"F0.imprint","IMPRINT",EDGE,{"derivedFrom":subQ0}),1.0]])]});}
            var Q177;
            {var subQ0=sQuery(id+"F0.wireOp",EDGE,"E3.1.1");var subQ1=sQuery(id+"F0.wireOp",EDGE,"E1");var subQ2=makeQuery(id+"F0.imprint","INTERSECT",VERTEX,{"derivedFrom":[subQ1,subQ0]});Q177=makeQuery(id+"F0.imprint","IMPRINT",FACE,{"disambiguationData":[TD([[makeQuery(id+"F0.imprint","IMPRINT",EDGE,{"disambiguationData":[TD([[subQ2,-1.0]])],"derivedFrom":subQ1}),-1.0]])]});}
            var Q178;
            {var subQ0=sQuery(id+"F0.wireOp",EDGE,"E3.98.2");var subQ1=sQuery(id+"F0.wireOp",EDGE,"E1");var subQ2=makeQuery(id+"F0.imprint","INTERSECT",VERTEX,{"derivedFrom":[subQ1,subQ0]});Q178=makeQuery(id+"F0.imprint","IMPRINT",FACE,{"disambiguationData":[TD([[makeQuery(id+"F0.imprint","IMPRINT",EDGE,{"disambiguationData":[TD([[subQ2,-1.0]])],"derivedFrom":subQ1}),-1.0]])]});}
            var Q179;
            {var subQ0=sQuery(id+"F0.wireOp",EDGE,"E3.29.0");Q179=makeQuery(id+"F0.imprint","IMPRINT",FACE,{"disambiguationData":[TD([[makeQuery(id+"F0.imprint","IMPRINT",EDGE,{"derivedFrom":subQ0}),1.0]])]});}
            var Q180;
            {var subQ0=sQuery(id+"F0.wireOp",EDGE,"E3.99.1");var subQ1=sQuery(id+"F0.wireOp",EDGE,"E1");var subQ2=makeQuery(id+"F0.imprint","INTERSECT",VERTEX,{"derivedFrom":[subQ1,subQ0]});Q180=makeQuery(id+"F0.imprint","IMPRINT",FACE,{"disambiguationData":[TD([[makeQuery(id+"F0.imprint","IMPRINT",EDGE,{"disambiguationData":[TD([[subQ2,-1.0]])],"derivedFrom":subQ1}),-1.0]])]});}
            var Q181;
            {var subQ0=sQuery(id+"F0.wireOp",EDGE,"E3.83.1");var subQ1=sQuery(id+"F0.wireOp",EDGE,"E1");var subQ2=makeQuery(id+"F0.imprint","INTERSECT",VERTEX,{"derivedFrom":[subQ1,subQ0]});Q181=makeQuery(id+"F0.imprint","IMPRINT",FACE,{"disambiguationData":[TD([[makeQuery(id+"F0.imprint","IMPRINT",EDGE,{"disambiguationData":[TD([[subQ2,-1.0]])],"derivedFrom":subQ1}),-1.0]])]});}
            var Q182;
            {var subQ0=sQuery(id+"F0.wireOp",EDGE,"E3.80.2");var subQ1=sQuery(id+"F0.wireOp",EDGE,"E1");var subQ2=makeQuery(id+"F0.imprint","INTERSECT",VERTEX,{"derivedFrom":[subQ1,subQ0]});Q182=makeQuery(id+"F0.imprint","IMPRINT",FACE,{"disambiguationData":[TD([[makeQuery(id+"F0.imprint","IMPRINT",EDGE,{"disambiguationData":[TD([[subQ2,-1.0]])],"derivedFrom":subQ1}),-1.0]])]});}
            var Q183;
            {var subQ0=sQuery(id+"F0.wireOp",EDGE,"E3.63.1");var subQ1=sQuery(id+"F0.wireOp",EDGE,"E1");var subQ2=makeQuery(id+"F0.imprint","INTERSECT",VERTEX,{"derivedFrom":[subQ1,subQ0]});Q183=makeQuery(id+"F0.imprint","IMPRINT",FACE,{"disambiguationData":[TD([[makeQuery(id+"F0.imprint","IMPRINT",EDGE,{"disambiguationData":[TD([[subQ2,-1.0]])],"derivedFrom":subQ1}),-1.0]])]});}
            var Q184;
            {var subQ0=sQuery(id+"F0.wireOp",EDGE,"E3.44.2");var subQ1=sQuery(id+"F0.wireOp",EDGE,"E1");var subQ2=makeQuery(id+"F0.imprint","INTERSECT",VERTEX,{"derivedFrom":[subQ1,subQ0]});Q184=makeQuery(id+"F0.imprint","IMPRINT",FACE,{"disambiguationData":[TD([[makeQuery(id+"F0.imprint","IMPRINT",EDGE,{"disambiguationData":[TD([[subQ2,-1.0]])],"derivedFrom":subQ1}),-1.0]])]});}
            var Q185;
            {var subQ0=sQuery(id+"F0.wireOp",EDGE,"E3.28.2");var subQ1=sQuery(id+"F0.wireOp",EDGE,"E1");var subQ2=makeQuery(id+"F0.imprint","INTERSECT",VERTEX,{"derivedFrom":[subQ1,subQ0]});Q185=makeQuery(id+"F0.imprint","IMPRINT",FACE,{"disambiguationData":[TD([[makeQuery(id+"F0.imprint","IMPRINT",EDGE,{"disambiguationData":[TD([[subQ2,-1.0]])],"derivedFrom":subQ1}),-1.0]])]});}
            var Q186;
            {var subQ0=sQuery(id+"F0.wireOp",EDGE,"E3.12.2");var subQ1=sQuery(id+"F0.wireOp",EDGE,"E1");var subQ2=makeQuery(id+"F0.imprint","INTERSECT",VERTEX,{"derivedFrom":[subQ1,subQ0]});Q186=makeQuery(id+"F0.imprint","IMPRINT",FACE,{"disambiguationData":[TD([[makeQuery(id+"F0.imprint","IMPRINT",EDGE,{"disambiguationData":[TD([[subQ2,-1.0]])],"derivedFrom":subQ1}),-1.0]])]});}
            var Q187;
            {var subQ0=sQuery(id+"F0.wireOp",EDGE,"E3.60.2");var subQ1=sQuery(id+"F0.wireOp",EDGE,"E1");var subQ2=makeQuery(id+"F0.imprint","INTERSECT",VERTEX,{"derivedFrom":[subQ1,subQ0]});Q187=makeQuery(id+"F0.imprint","IMPRINT",FACE,{"disambiguationData":[TD([[makeQuery(id+"F0.imprint","IMPRINT",EDGE,{"disambiguationData":[TD([[subQ2,-1.0]])],"derivedFrom":subQ1}),-1.0]])]});}
            var Q188;
            {var subQ0=sQuery(id+"F0.wireOp",EDGE,"E3.46.0");Q188=makeQuery(id+"F0.imprint","IMPRINT",FACE,{"disambiguationData":[TD([[makeQuery(id+"F0.imprint","IMPRINT",EDGE,{"derivedFrom":subQ0}),1.0]])]});}
            var Q189;
            {var subQ0=sQuery(id+"F0.wireOp",EDGE,"E3.1.2");var subQ1=sQuery(id+"F0.wireOp",EDGE,"E1");var subQ2=makeQuery(id+"F0.imprint","INTERSECT",VERTEX,{"derivedFrom":[subQ1,subQ0]});Q189=makeQuery(id+"F0.imprint","IMPRINT",FACE,{"disambiguationData":[TD([[makeQuery(id+"F0.imprint","IMPRINT",EDGE,{"disambiguationData":[TD([[subQ2,1.0]])],"derivedFrom":subQ1}),-1.0]])]});}
            var Q190;
            {var subQ0=sQuery(id+"F0.wireOp",EDGE,"E3.81.2");var subQ1=sQuery(id+"F0.wireOp",EDGE,"E1");var subQ2=makeQuery(id+"F0.imprint","INTERSECT",VERTEX,{"derivedFrom":[subQ1,subQ0]});Q190=makeQuery(id+"F0.imprint","IMPRINT",FACE,{"disambiguationData":[TD([[makeQuery(id+"F0.imprint","IMPRINT",EDGE,{"disambiguationData":[TD([[subQ2,-1.0]])],"derivedFrom":subQ1}),-1.0]])]});}
            var Q191;
            {var subQ0=sQuery(id+"F0.wireOp",EDGE,"E3.48.1");var subQ1=sQuery(id+"F0.wireOp",EDGE,"E1");var subQ2=makeQuery(id+"F0.imprint","INTERSECT",VERTEX,{"derivedFrom":[subQ1,subQ0]});Q191=makeQuery(id+"F0.imprint","IMPRINT",FACE,{"disambiguationData":[TD([[makeQuery(id+"F0.imprint","IMPRINT",EDGE,{"disambiguationData":[TD([[subQ2,-1.0]])],"derivedFrom":subQ1}),-1.0]])]});}
            var Q192;
            {var subQ0=sQuery(id+"F0.wireOp",EDGE,"E3.61.2");var subQ1=sQuery(id+"F0.wireOp",EDGE,"E1");var subQ2=makeQuery(id+"F0.imprint","INTERSECT",VERTEX,{"derivedFrom":[subQ1,subQ0]});Q192=makeQuery(id+"F0.imprint","IMPRINT",FACE,{"disambiguationData":[TD([[makeQuery(id+"F0.imprint","IMPRINT",EDGE,{"disambiguationData":[TD([[subQ2,-1.0]])],"derivedFrom":subQ1}),-1.0]])]});}
            var Q193;
            {var subQ0=sQuery(id+"F0.wireOp",EDGE,"E3.48.0");Q193=makeQuery(id+"F0.imprint","IMPRINT",FACE,{"disambiguationData":[TD([[makeQuery(id+"F0.imprint","IMPRINT",EDGE,{"derivedFrom":subQ0}),1.0]])]});}
            var Q194;
            {var subQ0=sQuery(id+"F0.wireOp",EDGE,"E3.32.0");Q194=makeQuery(id+"F0.imprint","IMPRINT",FACE,{"disambiguationData":[TD([[makeQuery(id+"F0.imprint","IMPRINT",EDGE,{"derivedFrom":subQ0}),1.0]])]});}
            var Q195;
            {var subQ0=sQuery(id+"F0.wireOp",EDGE,"E3.86.1");var subQ1=sQuery(id+"F0.wireOp",EDGE,"E1");var subQ2=makeQuery(id+"F0.imprint","INTERSECT",VERTEX,{"derivedFrom":[subQ1,subQ0]});Q195=makeQuery(id+"F0.imprint","IMPRINT",FACE,{"disambiguationData":[TD([[makeQuery(id+"F0.imprint","IMPRINT",EDGE,{"disambiguationData":[TD([[subQ2,-1.0]])],"derivedFrom":subQ1}),-1.0]])]});}
            var Q196;
            {var subQ0=sQuery(id+"F0.wireOp",EDGE,"E3.83.2");var subQ1=sQuery(id+"F0.wireOp",EDGE,"E1");var subQ2=makeQuery(id+"F0.imprint","INTERSECT",VERTEX,{"derivedFrom":[subQ1,subQ0]});Q196=makeQuery(id+"F0.imprint","IMPRINT",FACE,{"disambiguationData":[TD([[makeQuery(id+"F0.imprint","IMPRINT",EDGE,{"disambiguationData":[TD([[subQ2,-1.0]])],"derivedFrom":subQ1}),-1.0]])]});}
            var Q197;
            {var subQ0=sQuery(id+"F0.wireOp",EDGE,"E3.47.2");var subQ1=sQuery(id+"F0.wireOp",EDGE,"E1");var subQ2=makeQuery(id+"F0.imprint","INTERSECT",VERTEX,{"derivedFrom":[subQ1,subQ0]});Q197=makeQuery(id+"F0.imprint","IMPRINT",FACE,{"disambiguationData":[TD([[makeQuery(id+"F0.imprint","IMPRINT",EDGE,{"disambiguationData":[TD([[subQ2,-1.0]])],"derivedFrom":subQ1}),-1.0]])]});}
            var Q198;
            {var subQ0=sQuery(id+"F0.wireOp",EDGE,"E3.31.2");var subQ1=sQuery(id+"F0.wireOp",EDGE,"E1");var subQ2=makeQuery(id+"F0.imprint","INTERSECT",VERTEX,{"derivedFrom":[subQ1,subQ0]});Q198=makeQuery(id+"F0.imprint","IMPRINT",FACE,{"disambiguationData":[TD([[makeQuery(id+"F0.imprint","IMPRINT",EDGE,{"disambiguationData":[TD([[subQ2,-1.0]])],"derivedFrom":subQ1}),-1.0]])]});}
            var Q199;
            {var subQ0=sQuery(id+"F0.wireOp",EDGE,"E3.15.2");var subQ1=sQuery(id+"F0.wireOp",EDGE,"E1");var subQ2=makeQuery(id+"F0.imprint","INTERSECT",VERTEX,{"derivedFrom":[subQ1,subQ0]});Q199=makeQuery(id+"F0.imprint","IMPRINT",FACE,{"disambiguationData":[TD([[makeQuery(id+"F0.imprint","IMPRINT",EDGE,{"disambiguationData":[TD([[subQ2,-1.0]])],"derivedFrom":subQ1}),-1.0]])]});}
            var Q200;
            {var subQ0=sQuery(id+"F0.wireOp",EDGE,"E3.63.2");var subQ1=sQuery(id+"F0.wireOp",EDGE,"E1");var subQ2=makeQuery(id+"F0.imprint","INTERSECT",VERTEX,{"derivedFrom":[subQ1,subQ0]});Q200=makeQuery(id+"F0.imprint","IMPRINT",FACE,{"disambiguationData":[TD([[makeQuery(id+"F0.imprint","IMPRINT",EDGE,{"disambiguationData":[TD([[subQ2,-1.0]])],"derivedFrom":subQ1}),-1.0]])]});}
            var Q201;
            {var subQ0=sQuery(id+"F0.wireOp",EDGE,"E3.33.0");Q201=makeQuery(id+"F0.imprint","IMPRINT",FACE,{"disambiguationData":[TD([[makeQuery(id+"F0.imprint","IMPRINT",EDGE,{"derivedFrom":subQ0}),1.0]])]});}
            var Q202;
            {var subQ0=sQuery(id+"F0.wireOp",EDGE,"E3.84.2");var subQ1=sQuery(id+"F0.wireOp",EDGE,"E1");var subQ2=makeQuery(id+"F0.imprint","INTERSECT",VERTEX,{"derivedFrom":[subQ1,subQ0]});Q202=makeQuery(id+"F0.imprint","IMPRINT",FACE,{"disambiguationData":[TD([[makeQuery(id+"F0.imprint","IMPRINT",EDGE,{"disambiguationData":[TD([[subQ2,-1.0]])],"derivedFrom":subQ1}),-1.0]])]});}
            var Q203;
            {var subQ0=sQuery(id+"F0.wireOp",EDGE,"E3.51.1");var subQ1=sQuery(id+"F0.wireOp",EDGE,"E1");var subQ2=makeQuery(id+"F0.imprint","INTERSECT",VERTEX,{"derivedFrom":[subQ1,subQ0]});Q203=makeQuery(id+"F0.imprint","IMPRINT",FACE,{"disambiguationData":[TD([[makeQuery(id+"F0.imprint","IMPRINT",EDGE,{"disambiguationData":[TD([[subQ2,-1.0]])],"derivedFrom":subQ1}),-1.0]])]});}
            var Q204;
            {var subQ0=sQuery(id+"F0.wireOp",EDGE,"E3.32.2");var subQ1=sQuery(id+"F0.wireOp",EDGE,"E1");var subQ2=makeQuery(id+"F0.imprint","INTERSECT",VERTEX,{"derivedFrom":[subQ1,subQ0]});Q204=makeQuery(id+"F0.imprint","IMPRINT",FACE,{"disambiguationData":[TD([[makeQuery(id+"F0.imprint","IMPRINT",EDGE,{"disambiguationData":[TD([[subQ2,-1.0]])],"derivedFrom":subQ1}),-1.0]])]});}
            var Q205;
            {var subQ0=sQuery(id+"F0.wireOp",EDGE,"E3.16.2");var subQ1=sQuery(id+"F0.wireOp",EDGE,"E1");var subQ2=makeQuery(id+"F0.imprint","INTERSECT",VERTEX,{"derivedFrom":[subQ1,subQ0]});Q205=makeQuery(id+"F0.imprint","IMPRINT",FACE,{"disambiguationData":[TD([[makeQuery(id+"F0.imprint","IMPRINT",EDGE,{"disambiguationData":[TD([[subQ2,-1.0]])],"derivedFrom":subQ1}),-1.0]])]});}
            var Q206;
            {var subQ0=sQuery(id+"F0.wireOp",EDGE,"E3.64.2");var subQ1=sQuery(id+"F0.wireOp",EDGE,"E1");var subQ2=makeQuery(id+"F0.imprint","INTERSECT",VERTEX,{"derivedFrom":[subQ1,subQ0]});Q206=makeQuery(id+"F0.imprint","IMPRINT",FACE,{"disambiguationData":[TD([[makeQuery(id+"F0.imprint","IMPRINT",EDGE,{"disambiguationData":[TD([[subQ2,-1.0]])],"derivedFrom":subQ1}),-1.0]])]});}
            var Q207;
            {var subQ0=sQuery(id+"F0.wireOp",EDGE,"E3.82.0");Q207=makeQuery(id+"F0.imprint","IMPRINT",FACE,{"disambiguationData":[TD([[makeQuery(id+"F0.imprint","IMPRINT",EDGE,{"derivedFrom":subQ0}),1.0]])]});}
            var Q208;
            {var subQ0=sQuery(id+"F0.wireOp",EDGE,"E3.50.0");Q208=makeQuery(id+"F0.imprint","IMPRINT",FACE,{"disambiguationData":[TD([[makeQuery(id+"F0.imprint","IMPRINT",EDGE,{"derivedFrom":subQ0}),1.0]])]});}
            var Q209;
            {var subQ0=sQuery(id+"F0.wireOp",EDGE,"E3.20.1");var subQ1=sQuery(id+"F0.wireOp",EDGE,"E1");var subQ2=makeQuery(id+"F0.imprint","INTERSECT",VERTEX,{"derivedFrom":[subQ1,subQ0]});Q209=makeQuery(id+"F0.imprint","IMPRINT",FACE,{"disambiguationData":[TD([[makeQuery(id+"F0.imprint","IMPRINT",EDGE,{"disambiguationData":[TD([[subQ2,-1.0]])],"derivedFrom":subQ1}),-1.0]])]});}
            var Q210;
            {var subQ0=sQuery(id+"F0.wireOp",EDGE,"E3.88.1");var subQ1=sQuery(id+"F0.wireOp",EDGE,"E1");var subQ2=makeQuery(id+"F0.imprint","INTERSECT",VERTEX,{"derivedFrom":[subQ1,subQ0]});Q210=makeQuery(id+"F0.imprint","IMPRINT",FACE,{"disambiguationData":[TD([[makeQuery(id+"F0.imprint","IMPRINT",EDGE,{"disambiguationData":[TD([[subQ2,-1.0]])],"derivedFrom":subQ1}),-1.0]])]});}
            var Q211;
            {var subQ0=sQuery(id+"F0.wireOp",EDGE,"E3.85.2");var subQ1=sQuery(id+"F0.wireOp",EDGE,"E1");var subQ2=makeQuery(id+"F0.imprint","INTERSECT",VERTEX,{"derivedFrom":[subQ1,subQ0]});Q211=makeQuery(id+"F0.imprint","IMPRINT",FACE,{"disambiguationData":[TD([[makeQuery(id+"F0.imprint","IMPRINT",EDGE,{"disambiguationData":[TD([[subQ2,-1.0]])],"derivedFrom":subQ1}),-1.0]])]});}
            var Q212;
            {var subQ0=sQuery(id+"F0.wireOp",EDGE,"E3.33.2");var subQ1=sQuery(id+"F0.wireOp",EDGE,"E1");var subQ2=makeQuery(id+"F0.imprint","INTERSECT",VERTEX,{"derivedFrom":[subQ1,subQ0]});Q212=makeQuery(id+"F0.imprint","IMPRINT",FACE,{"disambiguationData":[TD([[makeQuery(id+"F0.imprint","IMPRINT",EDGE,{"disambiguationData":[TD([[subQ2,-1.0]])],"derivedFrom":subQ1}),-1.0]])]});}
            var Q213;
            {var subQ0=sQuery(id+"F0.wireOp",EDGE,"E3.65.2");var subQ1=sQuery(id+"F0.wireOp",EDGE,"E1");var subQ2=makeQuery(id+"F0.imprint","INTERSECT",VERTEX,{"derivedFrom":[subQ1,subQ0]});Q213=makeQuery(id+"F0.imprint","IMPRINT",FACE,{"disambiguationData":[TD([[makeQuery(id+"F0.imprint","IMPRINT",EDGE,{"disambiguationData":[TD([[subQ2,-1.0]])],"derivedFrom":subQ1}),-1.0]])]});}
            var Q214;
            {var subQ0=sQuery(id+"F0.wireOp",EDGE,"E3.19.0");Q214=makeQuery(id+"F0.imprint","IMPRINT",FACE,{"disambiguationData":[TD([[makeQuery(id+"F0.imprint","IMPRINT",EDGE,{"derivedFrom":subQ0}),1.0]])]});}
            var Q215;
            {var subQ0=sQuery(id+"F0.wireOp",EDGE,"E3.67.0");Q215=makeQuery(id+"F0.imprint","IMPRINT",FACE,{"disambiguationData":[TD([[makeQuery(id+"F0.imprint","IMPRINT",EDGE,{"derivedFrom":subQ0}),1.0]])]});}
            var Q216;
            {var subQ0=sQuery(id+"F0.wireOp",EDGE,"E3.21.1");var subQ1=sQuery(id+"F0.wireOp",EDGE,"E1");var subQ2=makeQuery(id+"F0.imprint","INTERSECT",VERTEX,{"derivedFrom":[subQ1,subQ0]});Q216=makeQuery(id+"F0.imprint","IMPRINT",FACE,{"disambiguationData":[TD([[makeQuery(id+"F0.imprint","IMPRINT",EDGE,{"disambiguationData":[TD([[subQ2,-1.0]])],"derivedFrom":subQ1}),-1.0]])]});}
            var Q217;
            {var subQ0=sQuery(id+"F0.wireOp",EDGE,"E3.86.2");var subQ1=sQuery(id+"F0.wireOp",EDGE,"E1");var subQ2=makeQuery(id+"F0.imprint","INTERSECT",VERTEX,{"derivedFrom":[subQ1,subQ0]});Q217=makeQuery(id+"F0.imprint","IMPRINT",FACE,{"disambiguationData":[TD([[makeQuery(id+"F0.imprint","IMPRINT",EDGE,{"disambiguationData":[TD([[subQ2,-1.0]])],"derivedFrom":subQ1}),-1.0]])]});}
            var Q218;
            {var subQ0=sQuery(id+"F0.wireOp",EDGE,"E3.53.1");var subQ1=sQuery(id+"F0.wireOp",EDGE,"E1");var subQ2=makeQuery(id+"F0.imprint","INTERSECT",VERTEX,{"derivedFrom":[subQ1,subQ0]});Q218=makeQuery(id+"F0.imprint","IMPRINT",FACE,{"disambiguationData":[TD([[makeQuery(id+"F0.imprint","IMPRINT",EDGE,{"disambiguationData":[TD([[subQ2,-1.0]])],"derivedFrom":subQ1}),-1.0]])]});}
            var Q219;
            {var subQ0=sQuery(id+"F0.wireOp",EDGE,"E3.50.2");var subQ1=sQuery(id+"F0.wireOp",EDGE,"E1");var subQ2=makeQuery(id+"F0.imprint","INTERSECT",VERTEX,{"derivedFrom":[subQ1,subQ0]});Q219=makeQuery(id+"F0.imprint","IMPRINT",FACE,{"disambiguationData":[TD([[makeQuery(id+"F0.imprint","IMPRINT",EDGE,{"disambiguationData":[TD([[subQ2,-1.0]])],"derivedFrom":subQ1}),-1.0]])]});}
            var Q220;
            {var subQ0=sQuery(id+"F0.wireOp",EDGE,"E3.34.2");var subQ1=sQuery(id+"F0.wireOp",EDGE,"E1");var subQ2=makeQuery(id+"F0.imprint","INTERSECT",VERTEX,{"derivedFrom":[subQ1,subQ0]});Q220=makeQuery(id+"F0.imprint","IMPRINT",FACE,{"disambiguationData":[TD([[makeQuery(id+"F0.imprint","IMPRINT",EDGE,{"disambiguationData":[TD([[subQ2,-1.0]])],"derivedFrom":subQ1}),-1.0]])]});}
            var Q221;
            {var subQ0=sQuery(id+"F0.wireOp",EDGE,"E3.18.2");var subQ1=sQuery(id+"F0.wireOp",EDGE,"E1");var subQ2=makeQuery(id+"F0.imprint","INTERSECT",VERTEX,{"derivedFrom":[subQ1,subQ0]});Q221=makeQuery(id+"F0.imprint","IMPRINT",FACE,{"disambiguationData":[TD([[makeQuery(id+"F0.imprint","IMPRINT",EDGE,{"disambiguationData":[TD([[subQ2,-1.0]])],"derivedFrom":subQ1}),-1.0]])]});}
            var Q222;
            {var subQ0=sQuery(id+"F0.wireOp",EDGE,"E3.66.2");var subQ1=sQuery(id+"F0.wireOp",EDGE,"E1");var subQ2=makeQuery(id+"F0.imprint","INTERSECT",VERTEX,{"derivedFrom":[subQ1,subQ0]});Q222=makeQuery(id+"F0.imprint","IMPRINT",FACE,{"disambiguationData":[TD([[makeQuery(id+"F0.imprint","IMPRINT",EDGE,{"disambiguationData":[TD([[subQ2,-1.0]])],"derivedFrom":subQ1}),-1.0]])]});}
            var Q223;
            {var subQ0=sQuery(id+"F0.wireOp",EDGE,"E3.68.0");Q223=makeQuery(id+"F0.imprint","IMPRINT",FACE,{"disambiguationData":[TD([[makeQuery(id+"F0.imprint","IMPRINT",EDGE,{"derivedFrom":subQ0}),1.0]])]});}
            var Q224;
            {var subQ0=sQuery(id+"F0.wireOp",EDGE,"E3.6.1");var subQ1=sQuery(id+"F0.wireOp",EDGE,"E1");var subQ2=makeQuery(id+"F0.imprint","INTERSECT",VERTEX,{"derivedFrom":[subQ1,subQ0]});Q224=makeQuery(id+"F0.imprint","IMPRINT",FACE,{"disambiguationData":[TD([[makeQuery(id+"F0.imprint","IMPRINT",EDGE,{"disambiguationData":[TD([[subQ2,-1.0]])],"derivedFrom":subQ1}),-1.0]])]});}
            var Q225;
            {var subQ0=sQuery(id+"F0.wireOp",EDGE,"E3.90.1");var subQ1=sQuery(id+"F0.wireOp",EDGE,"E1");var subQ2=makeQuery(id+"F0.imprint","INTERSECT",VERTEX,{"derivedFrom":[subQ1,subQ0]});Q225=makeQuery(id+"F0.imprint","IMPRINT",FACE,{"disambiguationData":[TD([[makeQuery(id+"F0.imprint","IMPRINT",EDGE,{"disambiguationData":[TD([[subQ2,-1.0]])],"derivedFrom":subQ1}),-1.0]])]});}
            var Q226;
            {var subQ0=sQuery(id+"F0.wireOp",EDGE,"E3.87.2");var subQ1=sQuery(id+"F0.wireOp",EDGE,"E1");var subQ2=makeQuery(id+"F0.imprint","INTERSECT",VERTEX,{"derivedFrom":[subQ1,subQ0]});Q226=makeQuery(id+"F0.imprint","IMPRINT",FACE,{"disambiguationData":[TD([[makeQuery(id+"F0.imprint","IMPRINT",EDGE,{"disambiguationData":[TD([[subQ2,-1.0]])],"derivedFrom":subQ1}),-1.0]])]});}
            var Q227;
            {var subQ0=sQuery(id+"F0.wireOp",EDGE,"E3.35.2");var subQ1=sQuery(id+"F0.wireOp",EDGE,"E1");var subQ2=makeQuery(id+"F0.imprint","INTERSECT",VERTEX,{"derivedFrom":[subQ1,subQ0]});Q227=makeQuery(id+"F0.imprint","IMPRINT",FACE,{"disambiguationData":[TD([[makeQuery(id+"F0.imprint","IMPRINT",EDGE,{"disambiguationData":[TD([[subQ2,-1.0]])],"derivedFrom":subQ1}),-1.0]])]});}
            var Q228;
            {var subQ0=sQuery(id+"F0.wireOp",EDGE,"E3.19.2");var subQ1=sQuery(id+"F0.wireOp",EDGE,"E1");var subQ2=makeQuery(id+"F0.imprint","INTERSECT",VERTEX,{"derivedFrom":[subQ1,subQ0]});Q228=makeQuery(id+"F0.imprint","IMPRINT",FACE,{"disambiguationData":[TD([[makeQuery(id+"F0.imprint","IMPRINT",EDGE,{"disambiguationData":[TD([[subQ2,-1.0]])],"derivedFrom":subQ1}),-1.0]])]});}
            var Q229;
            {var subQ0=sQuery(id+"F0.wireOp",EDGE,"E3.3.2");var subQ1=sQuery(id+"F0.wireOp",EDGE,"E1");var subQ2=makeQuery(id+"F0.imprint","INTERSECT",VERTEX,{"derivedFrom":[subQ1,subQ0]});Q229=makeQuery(id+"F0.imprint","IMPRINT",FACE,{"disambiguationData":[TD([[makeQuery(id+"F0.imprint","IMPRINT",EDGE,{"disambiguationData":[TD([[subQ2,-1.0]])],"derivedFrom":subQ1}),-1.0]])]});}
            var Q230;
            {var subQ0=sQuery(id+"F0.wireOp",EDGE,"E3.67.2");var subQ1=sQuery(id+"F0.wireOp",EDGE,"E1");var subQ2=makeQuery(id+"F0.imprint","INTERSECT",VERTEX,{"derivedFrom":[subQ1,subQ0]});Q230=makeQuery(id+"F0.imprint","IMPRINT",FACE,{"disambiguationData":[TD([[makeQuery(id+"F0.imprint","IMPRINT",EDGE,{"disambiguationData":[TD([[subQ2,-1.0]])],"derivedFrom":subQ1}),-1.0]])]});}
            var Q231;
            {var subQ0=sQuery(id+"F0.wireOp",EDGE,"E3.53.0");Q231=makeQuery(id+"F0.imprint","IMPRINT",FACE,{"disambiguationData":[TD([[makeQuery(id+"F0.imprint","IMPRINT",EDGE,{"derivedFrom":subQ0}),1.0]])]});}
            var Q232;
            {var subQ0=sQuery(id+"F0.wireOp",EDGE,"E3.37.0");Q232=makeQuery(id+"F0.imprint","IMPRINT",FACE,{"disambiguationData":[TD([[makeQuery(id+"F0.imprint","IMPRINT",EDGE,{"derivedFrom":subQ0}),1.0]])]});}
            var Q233;
            {var subQ0=sQuery(id+"F0.wireOp",EDGE,"E3.23.1");var subQ1=sQuery(id+"F0.wireOp",EDGE,"E1");var subQ2=makeQuery(id+"F0.imprint","INTERSECT",VERTEX,{"derivedFrom":[subQ1,subQ0]});Q233=makeQuery(id+"F0.imprint","IMPRINT",FACE,{"disambiguationData":[TD([[makeQuery(id+"F0.imprint","IMPRINT",EDGE,{"disambiguationData":[TD([[subQ2,-1.0]])],"derivedFrom":subQ1}),-1.0]])]});}
            var Q234;
            {var subQ0=sQuery(id+"F0.wireOp",EDGE,"E3.91.1");var subQ1=sQuery(id+"F0.wireOp",EDGE,"E1");var subQ2=makeQuery(id+"F0.imprint","INTERSECT",VERTEX,{"derivedFrom":[subQ1,subQ0]});Q234=makeQuery(id+"F0.imprint","IMPRINT",FACE,{"disambiguationData":[TD([[makeQuery(id+"F0.imprint","IMPRINT",EDGE,{"disambiguationData":[TD([[subQ2,-1.0]])],"derivedFrom":subQ1}),-1.0]])]});}
            var Q235;
            {var subQ0=sQuery(id+"F0.wireOp",EDGE,"E3.39.1");var subQ1=sQuery(id+"F0.wireOp",EDGE,"E1");var subQ2=makeQuery(id+"F0.imprint","INTERSECT",VERTEX,{"derivedFrom":[subQ1,subQ0]});Q235=makeQuery(id+"F0.imprint","IMPRINT",FACE,{"disambiguationData":[TD([[makeQuery(id+"F0.imprint","IMPRINT",EDGE,{"disambiguationData":[TD([[subQ2,-1.0]])],"derivedFrom":subQ1}),-1.0]])]});}
            var Q236;
            {var subQ0=sQuery(id+"F0.wireOp",EDGE,"E3.52.2");var subQ1=sQuery(id+"F0.wireOp",EDGE,"E1");var subQ2=makeQuery(id+"F0.imprint","INTERSECT",VERTEX,{"derivedFrom":[subQ1,subQ0]});Q236=makeQuery(id+"F0.imprint","IMPRINT",FACE,{"disambiguationData":[TD([[makeQuery(id+"F0.imprint","IMPRINT",EDGE,{"disambiguationData":[TD([[subQ2,-1.0]])],"derivedFrom":subQ1}),-1.0]])]});}
            var Q237;
            {var subQ0=sQuery(id+"F0.wireOp",EDGE,"E3.20.2");var subQ1=sQuery(id+"F0.wireOp",EDGE,"E1");var subQ2=makeQuery(id+"F0.imprint","INTERSECT",VERTEX,{"derivedFrom":[subQ1,subQ0]});Q237=makeQuery(id+"F0.imprint","IMPRINT",FACE,{"disambiguationData":[TD([[makeQuery(id+"F0.imprint","IMPRINT",EDGE,{"disambiguationData":[TD([[subQ2,-1.0]])],"derivedFrom":subQ1}),-1.0]])]});}
            var Q238;
            {var subQ0=sQuery(id+"F0.wireOp",EDGE,"E3.68.2");var subQ1=sQuery(id+"F0.wireOp",EDGE,"E1");var subQ2=makeQuery(id+"F0.imprint","INTERSECT",VERTEX,{"derivedFrom":[subQ1,subQ0]});Q238=makeQuery(id+"F0.imprint","IMPRINT",FACE,{"disambiguationData":[TD([[makeQuery(id+"F0.imprint","IMPRINT",EDGE,{"disambiguationData":[TD([[subQ2,-1.0]])],"derivedFrom":subQ1}),-1.0]])]});}
            var Q239;
            {var subQ0=sQuery(id+"F0.wireOp",EDGE,"E3.89.2");var subQ1=sQuery(id+"F0.wireOp",EDGE,"E1");var subQ2=makeQuery(id+"F0.imprint","INTERSECT",VERTEX,{"derivedFrom":[subQ1,subQ0]});Q239=makeQuery(id+"F0.imprint","IMPRINT",FACE,{"disambiguationData":[TD([[makeQuery(id+"F0.imprint","IMPRINT",EDGE,{"disambiguationData":[TD([[subQ2,-1.0]])],"derivedFrom":subQ1}),-1.0]])]});}
            var Q240;
            {var subQ0=sQuery(id+"F0.wireOp",EDGE,"E3.72.1");var subQ1=sQuery(id+"F0.wireOp",EDGE,"E1");var subQ2=makeQuery(id+"F0.imprint","INTERSECT",VERTEX,{"derivedFrom":[subQ1,subQ0]});Q240=makeQuery(id+"F0.imprint","IMPRINT",FACE,{"disambiguationData":[TD([[makeQuery(id+"F0.imprint","IMPRINT",EDGE,{"disambiguationData":[TD([[subQ2,-1.0]])],"derivedFrom":subQ1}),-1.0]])]});}
            var Q241;
            {var subQ0=sQuery(id+"F0.wireOp",EDGE,"E3.69.2");var subQ1=sQuery(id+"F0.wireOp",EDGE,"E1");var subQ2=makeQuery(id+"F0.imprint","INTERSECT",VERTEX,{"derivedFrom":[subQ1,subQ0]});Q241=makeQuery(id+"F0.imprint","IMPRINT",FACE,{"disambiguationData":[TD([[makeQuery(id+"F0.imprint","IMPRINT",EDGE,{"disambiguationData":[TD([[subQ2,-1.0]])],"derivedFrom":subQ1}),-1.0]])]});}
            var Q242;
            {var subQ0=sQuery(id+"F0.wireOp",EDGE,"E3.37.2");var subQ1=sQuery(id+"F0.wireOp",EDGE,"E1");var subQ2=makeQuery(id+"F0.imprint","INTERSECT",VERTEX,{"derivedFrom":[subQ1,subQ0]});Q242=makeQuery(id+"F0.imprint","IMPRINT",FACE,{"disambiguationData":[TD([[makeQuery(id+"F0.imprint","IMPRINT",EDGE,{"disambiguationData":[TD([[subQ2,-1.0]])],"derivedFrom":subQ1}),-1.0]])]});}
            var Q243;
            {var subQ0=sQuery(id+"F0.wireOp",EDGE,"E3.38.0");Q243=makeQuery(id+"F0.imprint","IMPRINT",FACE,{"disambiguationData":[TD([[makeQuery(id+"F0.imprint","IMPRINT",EDGE,{"derivedFrom":subQ0}),1.0]])]});}
            var Q244;
            {var subQ0=sQuery(id+"F0.wireOp",EDGE,"E3.9.1");var subQ1=sQuery(id+"F0.wireOp",EDGE,"E1");var subQ2=makeQuery(id+"F0.imprint","INTERSECT",VERTEX,{"derivedFrom":[subQ1,subQ0]});Q244=makeQuery(id+"F0.imprint","IMPRINT",FACE,{"disambiguationData":[TD([[makeQuery(id+"F0.imprint","IMPRINT",EDGE,{"disambiguationData":[TD([[subQ2,-1.0]])],"derivedFrom":subQ1}),-1.0]])]});}
            var Q245;
            {var subQ0=sQuery(id+"F0.wireOp",EDGE,"E3.6.2");var subQ1=sQuery(id+"F0.wireOp",EDGE,"E1");var subQ2=makeQuery(id+"F0.imprint","INTERSECT",VERTEX,{"derivedFrom":[subQ1,subQ0]});Q245=makeQuery(id+"F0.imprint","IMPRINT",FACE,{"disambiguationData":[TD([[makeQuery(id+"F0.imprint","IMPRINT",EDGE,{"disambiguationData":[TD([[subQ2,-1.0]])],"derivedFrom":subQ1}),-1.0]])]});}
            var Q246;
            {var subQ0=sQuery(id+"F0.wireOp",EDGE,"E3.90.2");var subQ1=sQuery(id+"F0.wireOp",EDGE,"E1");var subQ2=makeQuery(id+"F0.imprint","INTERSECT",VERTEX,{"derivedFrom":[subQ1,subQ0]});Q246=makeQuery(id+"F0.imprint","IMPRINT",FACE,{"disambiguationData":[TD([[makeQuery(id+"F0.imprint","IMPRINT",EDGE,{"disambiguationData":[TD([[subQ2,-1.0]])],"derivedFrom":subQ1}),-1.0]])]});}
            var Q247;
            {var subQ0=sQuery(id+"F0.wireOp",EDGE,"E3.73.1");var subQ1=sQuery(id+"F0.wireOp",EDGE,"E1");var subQ2=makeQuery(id+"F0.imprint","INTERSECT",VERTEX,{"derivedFrom":[subQ1,subQ0]});Q247=makeQuery(id+"F0.imprint","IMPRINT",FACE,{"disambiguationData":[TD([[makeQuery(id+"F0.imprint","IMPRINT",EDGE,{"disambiguationData":[TD([[subQ2,-1.0]])],"derivedFrom":subQ1}),-1.0]])]});}
            var Q248;
            {var subQ0=sQuery(id+"F0.wireOp",EDGE,"E3.70.2");var subQ1=sQuery(id+"F0.wireOp",EDGE,"E1");var subQ2=makeQuery(id+"F0.imprint","INTERSECT",VERTEX,{"derivedFrom":[subQ1,subQ0]});Q248=makeQuery(id+"F0.imprint","IMPRINT",FACE,{"disambiguationData":[TD([[makeQuery(id+"F0.imprint","IMPRINT",EDGE,{"disambiguationData":[TD([[subQ2,-1.0]])],"derivedFrom":subQ1}),-1.0]])]});}
            var Q249;
            {var subQ0=sQuery(id+"F0.wireOp",EDGE,"E3.38.2");var subQ1=sQuery(id+"F0.wireOp",EDGE,"E1");var subQ2=makeQuery(id+"F0.imprint","INTERSECT",VERTEX,{"derivedFrom":[subQ1,subQ0]});Q249=makeQuery(id+"F0.imprint","IMPRINT",FACE,{"disambiguationData":[TD([[makeQuery(id+"F0.imprint","IMPRINT",EDGE,{"disambiguationData":[TD([[subQ2,-1.0]])],"derivedFrom":subQ1}),-1.0]])]});}
            var Q250;
            {var subQ0=sQuery(id+"F0.wireOp",EDGE,"E3.93.1");var subQ1=sQuery(id+"F0.wireOp",EDGE,"E1");var subQ2=makeQuery(id+"F0.imprint","INTERSECT",VERTEX,{"derivedFrom":[subQ1,subQ0]});Q250=makeQuery(id+"F0.imprint","IMPRINT",FACE,{"disambiguationData":[TD([[makeQuery(id+"F0.imprint","IMPRINT",EDGE,{"disambiguationData":[TD([[subQ2,-1.0]])],"derivedFrom":subQ1}),-1.0]])]});}
            var Q251;
            {var subQ0=sQuery(id+"F0.wireOp",EDGE,"E3.77.1");var subQ1=sQuery(id+"F0.wireOp",EDGE,"E1");var subQ2=makeQuery(id+"F0.imprint","INTERSECT",VERTEX,{"derivedFrom":[subQ1,subQ0]});Q251=makeQuery(id+"F0.imprint","IMPRINT",FACE,{"disambiguationData":[TD([[makeQuery(id+"F0.imprint","IMPRINT",EDGE,{"disambiguationData":[TD([[subQ2,-1.0]])],"derivedFrom":subQ1}),-1.0]])]});}
            var Q252;
            {var subQ0=sQuery(id+"F0.wireOp",EDGE,"E3.71.0");Q252=makeQuery(id+"F0.imprint","IMPRINT",FACE,{"disambiguationData":[TD([[makeQuery(id+"F0.imprint","IMPRINT",EDGE,{"derivedFrom":subQ0}),1.0]])]});}
            var Q253;
            {var subQ0=sQuery(id+"F0.wireOp",EDGE,"E3.23.2");var subQ1=sQuery(id+"F0.wireOp",EDGE,"E1");var subQ2=makeQuery(id+"F0.imprint","INTERSECT",VERTEX,{"derivedFrom":[subQ1,subQ0]});Q253=makeQuery(id+"F0.imprint","IMPRINT",FACE,{"disambiguationData":[TD([[makeQuery(id+"F0.imprint","IMPRINT",EDGE,{"disambiguationData":[TD([[subQ2,-1.0]])],"derivedFrom":subQ1}),-1.0]])]});}
            var Q254;
            {var subQ0=sQuery(id+"F0.wireOp",EDGE,"E3.7.2");var subQ1=sQuery(id+"F0.wireOp",EDGE,"E1");var subQ2=makeQuery(id+"F0.imprint","INTERSECT",VERTEX,{"derivedFrom":[subQ1,subQ0]});Q254=makeQuery(id+"F0.imprint","IMPRINT",FACE,{"disambiguationData":[TD([[makeQuery(id+"F0.imprint","IMPRINT",EDGE,{"disambiguationData":[TD([[subQ2,-1.0]])],"derivedFrom":subQ1}),-1.0]])]});}
            var Q255;
            {var subQ0=sQuery(id+"F0.wireOp",EDGE,"E3.91.2");var subQ1=sQuery(id+"F0.wireOp",EDGE,"E1");var subQ2=makeQuery(id+"F0.imprint","INTERSECT",VERTEX,{"derivedFrom":[subQ1,subQ0]});Q255=makeQuery(id+"F0.imprint","IMPRINT",FACE,{"disambiguationData":[TD([[makeQuery(id+"F0.imprint","IMPRINT",EDGE,{"disambiguationData":[TD([[subQ2,-1.0]])],"derivedFrom":subQ1}),-1.0]])]});}
            var Q256;
            {var subQ0=sQuery(id+"F0.wireOp",EDGE,"E3.55.2");var subQ1=sQuery(id+"F0.wireOp",EDGE,"E1");var subQ2=makeQuery(id+"F0.imprint","INTERSECT",VERTEX,{"derivedFrom":[subQ1,subQ0]});Q256=makeQuery(id+"F0.imprint","IMPRINT",FACE,{"disambiguationData":[TD([[makeQuery(id+"F0.imprint","IMPRINT",EDGE,{"disambiguationData":[TD([[subQ2,-1.0]])],"derivedFrom":subQ1}),-1.0]])]});}
            var Q257;
            {var subQ0=sQuery(id+"F0.wireOp",EDGE,"E3.56.0");Q257=makeQuery(id+"F0.imprint","IMPRINT",FACE,{"disambiguationData":[TD([[makeQuery(id+"F0.imprint","IMPRINT",EDGE,{"derivedFrom":subQ0}),1.0]])]});}
            var Q258;
            {var subQ0=sQuery(id+"F0.wireOp",EDGE,"E3.78.1");var subQ1=sQuery(id+"F0.wireOp",EDGE,"E1");var subQ2=makeQuery(id+"F0.imprint","INTERSECT",VERTEX,{"derivedFrom":[subQ1,subQ0]});Q258=makeQuery(id+"F0.imprint","IMPRINT",FACE,{"disambiguationData":[TD([[makeQuery(id+"F0.imprint","IMPRINT",EDGE,{"disambiguationData":[TD([[subQ2,-1.0]])],"derivedFrom":subQ1}),-1.0]])]});}
            var Q259;
            {var subQ0=sQuery(id+"F0.wireOp",EDGE,"E3.88.0");Q259=makeQuery(id+"F0.imprint","IMPRINT",FACE,{"disambiguationData":[TD([[makeQuery(id+"F0.imprint","IMPRINT",EDGE,{"derivedFrom":subQ0}),1.0]])]});}
            var Q260;
            {var subQ0=sQuery(id+"F0.wireOp",EDGE,"E3.26.1");var subQ1=sQuery(id+"F0.wireOp",EDGE,"E1");var subQ2=makeQuery(id+"F0.imprint","INTERSECT",VERTEX,{"derivedFrom":[subQ1,subQ0]});Q260=makeQuery(id+"F0.imprint","IMPRINT",FACE,{"disambiguationData":[TD([[makeQuery(id+"F0.imprint","IMPRINT",EDGE,{"disambiguationData":[TD([[subQ2,-1.0]])],"derivedFrom":subQ1}),-1.0]])]});}
            var Q261;
            {var subQ0=sQuery(id+"F0.wireOp",EDGE,"E3.10.1");var subQ1=sQuery(id+"F0.wireOp",EDGE,"E1");var subQ2=makeQuery(id+"F0.imprint","INTERSECT",VERTEX,{"derivedFrom":[subQ1,subQ0]});Q261=makeQuery(id+"F0.imprint","IMPRINT",FACE,{"disambiguationData":[TD([[makeQuery(id+"F0.imprint","IMPRINT",EDGE,{"disambiguationData":[TD([[subQ2,-1.0]])],"derivedFrom":subQ1}),-1.0]])]});}
            var Q262;
            {var subQ0=sQuery(id+"F0.wireOp",EDGE,"E3.72.2");var subQ1=sQuery(id+"F0.wireOp",EDGE,"E1");var subQ2=makeQuery(id+"F0.imprint","INTERSECT",VERTEX,{"derivedFrom":[subQ1,subQ0]});Q262=makeQuery(id+"F0.imprint","IMPRINT",FACE,{"disambiguationData":[TD([[makeQuery(id+"F0.imprint","IMPRINT",EDGE,{"disambiguationData":[TD([[subQ2,-1.0]])],"derivedFrom":subQ1}),-1.0]])]});}
            var Q263;
            {var subQ0=sQuery(id+"F0.wireOp",EDGE,"E3.40.2");var subQ1=sQuery(id+"F0.wireOp",EDGE,"E1");var subQ2=makeQuery(id+"F0.imprint","INTERSECT",VERTEX,{"derivedFrom":[subQ1,subQ0]});Q263=makeQuery(id+"F0.imprint","IMPRINT",FACE,{"disambiguationData":[TD([[makeQuery(id+"F0.imprint","IMPRINT",EDGE,{"disambiguationData":[TD([[subQ2,-1.0]])],"derivedFrom":subQ1}),-1.0]])]});}
            var Q264;
            {var subQ0=sQuery(id+"F0.wireOp",EDGE,"E3.25.0");Q264=makeQuery(id+"F0.imprint","IMPRINT",FACE,{"disambiguationData":[TD([[makeQuery(id+"F0.imprint","IMPRINT",EDGE,{"derivedFrom":subQ0}),1.0]])]});}
            var Q265;
            {var subQ0=sQuery(id+"F0.wireOp",EDGE,"E3.89.0");Q265=makeQuery(id+"F0.imprint","IMPRINT",FACE,{"disambiguationData":[TD([[makeQuery(id+"F0.imprint","IMPRINT",EDGE,{"derivedFrom":subQ0}),1.0]])]});}
            var Q266;
            {var subQ0=sQuery(id+"F0.wireOp",EDGE,"E3.73.0");Q266=makeQuery(id+"F0.imprint","IMPRINT",FACE,{"disambiguationData":[TD([[makeQuery(id+"F0.imprint","IMPRINT",EDGE,{"derivedFrom":subQ0}),1.0]])]});}
            var Q267;
            {var subQ0=sQuery(id+"F0.wireOp",EDGE,"E3.59.1");var subQ1=sQuery(id+"F0.wireOp",EDGE,"E1");var subQ2=makeQuery(id+"F0.imprint","INTERSECT",VERTEX,{"derivedFrom":[subQ1,subQ0]});Q267=makeQuery(id+"F0.imprint","IMPRINT",FACE,{"disambiguationData":[TD([[makeQuery(id+"F0.imprint","IMPRINT",EDGE,{"disambiguationData":[TD([[subQ2,-1.0]])],"derivedFrom":subQ1}),-1.0]])]});}
            var Q268;
            {var subQ0=sQuery(id+"F0.wireOp",EDGE,"E3.11.1");var subQ1=sQuery(id+"F0.wireOp",EDGE,"E1");var subQ2=makeQuery(id+"F0.imprint","INTERSECT",VERTEX,{"derivedFrom":[subQ1,subQ0]});Q268=makeQuery(id+"F0.imprint","IMPRINT",FACE,{"disambiguationData":[TD([[makeQuery(id+"F0.imprint","IMPRINT",EDGE,{"disambiguationData":[TD([[subQ2,-1.0]])],"derivedFrom":subQ1}),-1.0]])]});}
            var Q269;
            {var subQ0=sQuery(id+"F0.wireOp",EDGE,"E3.8.2");var subQ1=sQuery(id+"F0.wireOp",EDGE,"E1");var subQ2=makeQuery(id+"F0.imprint","INTERSECT",VERTEX,{"derivedFrom":[subQ1,subQ0]});Q269=makeQuery(id+"F0.imprint","IMPRINT",FACE,{"disambiguationData":[TD([[makeQuery(id+"F0.imprint","IMPRINT",EDGE,{"disambiguationData":[TD([[subQ2,-1.0]])],"derivedFrom":subQ1}),-1.0]])]});}
            var Q270;
            {var subQ0=sQuery(id+"F0.wireOp",EDGE,"E3.42.0");Q270=makeQuery(id+"F0.imprint","IMPRINT",FACE,{"disambiguationData":[TD([[makeQuery(id+"F0.imprint","IMPRINT",EDGE,{"derivedFrom":subQ0}),1.0]])]});}
            var Q271;
            {var subQ0=sQuery(id+"F0.wireOp",EDGE,"E3.44.1");var subQ1=sQuery(id+"F0.wireOp",EDGE,"E1");var subQ2=makeQuery(id+"F0.imprint","INTERSECT",VERTEX,{"derivedFrom":[subQ1,subQ0]});Q271=makeQuery(id+"F0.imprint","IMPRINT",FACE,{"disambiguationData":[TD([[makeQuery(id+"F0.imprint","IMPRINT",EDGE,{"disambiguationData":[TD([[subQ2,-1.0]])],"derivedFrom":subQ1}),-1.0]])]});}
            var Q272;
            {var subQ0=sQuery(id+"F0.wireOp",EDGE,"E3.28.1");var subQ1=sQuery(id+"F0.wireOp",EDGE,"E1");var subQ2=makeQuery(id+"F0.imprint","INTERSECT",VERTEX,{"derivedFrom":[subQ1,subQ0]});Q272=makeQuery(id+"F0.imprint","IMPRINT",FACE,{"disambiguationData":[TD([[makeQuery(id+"F0.imprint","IMPRINT",EDGE,{"disambiguationData":[TD([[subQ2,-1.0]])],"derivedFrom":subQ1}),-1.0]])]});}
            var Q273;
            {var subQ0=sQuery(id+"F0.wireOp",EDGE,"E3.25.2");var subQ1=sQuery(id+"F0.wireOp",EDGE,"E1");var subQ2=makeQuery(id+"F0.imprint","INTERSECT",VERTEX,{"derivedFrom":[subQ1,subQ0]});Q273=makeQuery(id+"F0.imprint","IMPRINT",FACE,{"disambiguationData":[TD([[makeQuery(id+"F0.imprint","IMPRINT",EDGE,{"disambiguationData":[TD([[subQ2,-1.0]])],"derivedFrom":subQ1}),-1.0]])]});}
            var Q274;
            {var subQ0=sQuery(id+"F0.wireOp",EDGE,"E3.9.2");var subQ1=sQuery(id+"F0.wireOp",EDGE,"E1");var subQ2=makeQuery(id+"F0.imprint","INTERSECT",VERTEX,{"derivedFrom":[subQ1,subQ0]});Q274=makeQuery(id+"F0.imprint","IMPRINT",FACE,{"disambiguationData":[TD([[makeQuery(id+"F0.imprint","IMPRINT",EDGE,{"disambiguationData":[TD([[subQ2,-1.0]])],"derivedFrom":subQ1}),-1.0]])]});}
            var Q275;
            {var subQ0=sQuery(id+"F0.wireOp",EDGE,"E3.77.2");var subQ1=sQuery(id+"F0.wireOp",EDGE,"E1");var subQ2=makeQuery(id+"F0.imprint","INTERSECT",VERTEX,{"derivedFrom":[subQ1,subQ0]});Q275=makeQuery(id+"F0.imprint","IMPRINT",FACE,{"disambiguationData":[TD([[makeQuery(id+"F0.imprint","IMPRINT",EDGE,{"disambiguationData":[TD([[subQ2,-1.0]])],"derivedFrom":subQ1}),-1.0]])]});}
            var Q276;
            {var subQ0=sQuery(id+"F0.wireOp",EDGE,"E3.57.2");var subQ1=sQuery(id+"F0.wireOp",EDGE,"E1");var subQ2=makeQuery(id+"F0.imprint","INTERSECT",VERTEX,{"derivedFrom":[subQ1,subQ0]});Q276=makeQuery(id+"F0.imprint","IMPRINT",FACE,{"disambiguationData":[TD([[makeQuery(id+"F0.imprint","IMPRINT",EDGE,{"disambiguationData":[TD([[subQ2,-1.0]])],"derivedFrom":subQ1}),-1.0]])]});}
            var Q277;
            {var subQ0=sQuery(id+"F0.wireOp",EDGE,"E3.41.2");var subQ1=sQuery(id+"F0.wireOp",EDGE,"E1");var subQ2=makeQuery(id+"F0.imprint","INTERSECT",VERTEX,{"derivedFrom":[subQ1,subQ0]});Q277=makeQuery(id+"F0.imprint","IMPRINT",FACE,{"disambiguationData":[TD([[makeQuery(id+"F0.imprint","IMPRINT",EDGE,{"disambiguationData":[TD([[subQ2,-1.0]])],"derivedFrom":subQ1}),-1.0]])]});}
            var Q278;
            {var subQ0=sQuery(id+"F0.wireOp",EDGE,"E3.43.0");Q278=makeQuery(id+"F0.imprint","IMPRINT",FACE,{"disambiguationData":[TD([[makeQuery(id+"F0.imprint","IMPRINT",EDGE,{"derivedFrom":subQ0}),1.0]])]});}
            var Q279;
            {var subQ0=sQuery(id+"F0.wireOp",EDGE,"E3.27.0");Q279=makeQuery(id+"F0.imprint","IMPRINT",FACE,{"disambiguationData":[TD([[makeQuery(id+"F0.imprint","IMPRINT",EDGE,{"derivedFrom":subQ0}),1.0]])]});}
            var Q280;
            {var subQ0=sQuery(id+"F0.wireOp",EDGE,"E3.75.0");Q280=makeQuery(id+"F0.imprint","IMPRINT",FACE,{"disambiguationData":[TD([[makeQuery(id+"F0.imprint","IMPRINT",EDGE,{"derivedFrom":subQ0}),1.0]])]});}
            var Q281;
            {var subQ0=sQuery(id+"F0.wireOp",EDGE,"E3.45.1");var subQ1=sQuery(id+"F0.wireOp",EDGE,"E1");var subQ2=makeQuery(id+"F0.imprint","INTERSECT",VERTEX,{"derivedFrom":[subQ1,subQ0]});Q281=makeQuery(id+"F0.imprint","IMPRINT",FACE,{"disambiguationData":[TD([[makeQuery(id+"F0.imprint","IMPRINT",EDGE,{"disambiguationData":[TD([[subQ2,-1.0]])],"derivedFrom":subQ1}),-1.0]])]});}
            var Q282;
            {var subQ0=sQuery(id+"F0.wireOp",EDGE,"E3.29.1");var subQ1=sQuery(id+"F0.wireOp",EDGE,"E1");var subQ2=makeQuery(id+"F0.imprint","INTERSECT",VERTEX,{"derivedFrom":[subQ1,subQ0]});Q282=makeQuery(id+"F0.imprint","IMPRINT",FACE,{"disambiguationData":[TD([[makeQuery(id+"F0.imprint","IMPRINT",EDGE,{"disambiguationData":[TD([[subQ2,-1.0]])],"derivedFrom":subQ1}),-1.0]])]});}
            var Q283;
            {var subQ0=sQuery(id+"F0.wireOp",EDGE,"E3.10.2");var subQ1=sQuery(id+"F0.wireOp",EDGE,"E1");var subQ2=makeQuery(id+"F0.imprint","INTERSECT",VERTEX,{"derivedFrom":[subQ1,subQ0]});Q283=makeQuery(id+"F0.imprint","IMPRINT",FACE,{"disambiguationData":[TD([[makeQuery(id+"F0.imprint","IMPRINT",EDGE,{"disambiguationData":[TD([[subQ2,-1.0]])],"derivedFrom":subQ1}),-1.0]])]});}
            var Q284;
            {var subQ0=sQuery(id+"F0.wireOp",EDGE,"E3.94.2");var subQ1=sQuery(id+"F0.wireOp",EDGE,"E1");var subQ2=makeQuery(id+"F0.imprint","INTERSECT",VERTEX,{"derivedFrom":[subQ1,subQ0]});Q284=makeQuery(id+"F0.imprint","IMPRINT",FACE,{"disambiguationData":[TD([[makeQuery(id+"F0.imprint","IMPRINT",EDGE,{"disambiguationData":[TD([[subQ2,-1.0]])],"derivedFrom":subQ1}),-1.0]])]});}
            var Q285;
            {var subQ0=sQuery(id+"F0.wireOp",EDGE,"E3.42.2");var subQ1=sQuery(id+"F0.wireOp",EDGE,"E1");var subQ2=makeQuery(id+"F0.imprint","INTERSECT",VERTEX,{"derivedFrom":[subQ1,subQ0]});Q285=makeQuery(id+"F0.imprint","IMPRINT",FACE,{"disambiguationData":[TD([[makeQuery(id+"F0.imprint","IMPRINT",EDGE,{"disambiguationData":[TD([[subQ2,-1.0]])],"derivedFrom":subQ1}),-1.0]])]});}
            var Q286;
            {var subQ0=sQuery(id+"F0.wireOp",EDGE,"E3.46.1");var subQ1=sQuery(id+"F0.wireOp",EDGE,"E1");var subQ2=makeQuery(id+"F0.imprint","INTERSECT",VERTEX,{"derivedFrom":[subQ1,subQ0]});Q286=makeQuery(id+"F0.imprint","IMPRINT",FACE,{"disambiguationData":[TD([[makeQuery(id+"F0.imprint","IMPRINT",EDGE,{"disambiguationData":[TD([[subQ2,-1.0]])],"derivedFrom":subQ1}),-1.0]])]});}
            var Q287;
            {var subQ0=sQuery(id+"F0.wireOp",EDGE,"E3.30.1");var subQ1=sQuery(id+"F0.wireOp",EDGE,"E1");var subQ2=makeQuery(id+"F0.imprint","INTERSECT",VERTEX,{"derivedFrom":[subQ1,subQ0]});Q287=makeQuery(id+"F0.imprint","IMPRINT",FACE,{"disambiguationData":[TD([[makeQuery(id+"F0.imprint","IMPRINT",EDGE,{"disambiguationData":[TD([[subQ2,-1.0]])],"derivedFrom":subQ1}),-1.0]])]});}
            var Q288;
            {var subQ0=sQuery(id+"F0.wireOp",EDGE,"E3.11.2");var subQ1=sQuery(id+"F0.wireOp",EDGE,"E1");var subQ2=makeQuery(id+"F0.imprint","INTERSECT",VERTEX,{"derivedFrom":[subQ1,subQ0]});Q288=makeQuery(id+"F0.imprint","IMPRINT",FACE,{"disambiguationData":[TD([[makeQuery(id+"F0.imprint","IMPRINT",EDGE,{"disambiguationData":[TD([[subQ2,-1.0]])],"derivedFrom":subQ1}),-1.0]])]});}
            var Q289;
            {var subQ0=sQuery(id+"F0.wireOp",EDGE,"E3.95.2");var subQ1=sQuery(id+"F0.wireOp",EDGE,"E1");var subQ2=makeQuery(id+"F0.imprint","INTERSECT",VERTEX,{"derivedFrom":[subQ1,subQ0]});Q289=makeQuery(id+"F0.imprint","IMPRINT",FACE,{"disambiguationData":[TD([[makeQuery(id+"F0.imprint","IMPRINT",EDGE,{"disambiguationData":[TD([[subQ2,-1.0]])],"derivedFrom":subQ1}),-1.0]])]});}
            var Q290;
            {var subQ0=sQuery(id+"F0.wireOp",EDGE,"E3.79.2");var subQ1=sQuery(id+"F0.wireOp",EDGE,"E1");var subQ2=makeQuery(id+"F0.imprint","INTERSECT",VERTEX,{"derivedFrom":[subQ1,subQ0]});Q290=makeQuery(id+"F0.imprint","IMPRINT",FACE,{"disambiguationData":[TD([[makeQuery(id+"F0.imprint","IMPRINT",EDGE,{"disambiguationData":[TD([[subQ2,-1.0]])],"derivedFrom":subQ1}),-1.0]])]});}
            var Q291;
            {var subQ0=sQuery(id+"F0.wireOp",EDGE,"E3.75.1");var subQ1=sQuery(id+"F0.wireOp",EDGE,"E1");var subQ2=makeQuery(id+"F0.imprint","INTERSECT",VERTEX,{"derivedFrom":[subQ1,subQ0]});Q291=makeQuery(id+"F0.imprint","IMPRINT",FACE,{"disambiguationData":[TD([[makeQuery(id+"F0.imprint","IMPRINT",EDGE,{"disambiguationData":[TD([[subQ2,1.0]])],"derivedFrom":subQ1}),-1.0]])]});}
            var Q292;
            {var subQ0=sQuery(id+"F0.wireOp",EDGE,"E3.59.2");var subQ1=sQuery(id+"F0.wireOp",EDGE,"E1");var subQ2=makeQuery(id+"F0.imprint","INTERSECT",VERTEX,{"derivedFrom":[subQ1,subQ0]});Q292=makeQuery(id+"F0.imprint","IMPRINT",FACE,{"disambiguationData":[TD([[makeQuery(id+"F0.imprint","IMPRINT",EDGE,{"disambiguationData":[TD([[subQ2,-1.0]])],"derivedFrom":subQ1}),-1.0]])]});}
            var Q293;
            {var subQ0=sQuery(id+"F0.wireOp",EDGE,"E3.43.2");var subQ1=sQuery(id+"F0.wireOp",EDGE,"E1");var subQ2=makeQuery(id+"F0.imprint","INTERSECT",VERTEX,{"derivedFrom":[subQ1,subQ0]});Q293=makeQuery(id+"F0.imprint","IMPRINT",FACE,{"disambiguationData":[TD([[makeQuery(id+"F0.imprint","IMPRINT",EDGE,{"disambiguationData":[TD([[subQ2,-1.0]])],"derivedFrom":subQ1}),-1.0]])]});}
            var Q294;
            {var subQ0=sQuery(id+"F0.wireOp",EDGE,"E3.2.0");Q294=makeQuery(id+"F0.imprint","IMPRINT",FACE,{"disambiguationData":[TD([[makeQuery(id+"F0.imprint","IMPRINT",EDGE,{"derivedFrom":subQ0}),1.0]])]});}
            var Q295;
            {var subQ0=sQuery(id+"F0.wireOp",EDGE,"E3.4.0");Q295=makeQuery(id+"F0.imprint","IMPRINT",FACE,{"disambiguationData":[TD([[makeQuery(id+"F0.imprint","IMPRINT",EDGE,{"derivedFrom":subQ0}),1.0]])]});}
            var Q296;
            {var subQ0=sQuery(id+"F0.wireOp",EDGE,"E3.7.0");Q296=makeQuery(id+"F0.imprint","IMPRINT",FACE,{"disambiguationData":[TD([[makeQuery(id+"F0.imprint","IMPRINT",EDGE,{"derivedFrom":subQ0}),1.0]])]});}
            var Q297;
            {var subQ0=sQuery(id+"F0.wireOp",EDGE,"E3.8.0");Q297=makeQuery(id+"F0.imprint","IMPRINT",FACE,{"disambiguationData":[TD([[makeQuery(id+"F0.imprint","IMPRINT",EDGE,{"derivedFrom":subQ0}),1.0]])]});}
            var Q298;
            {var subQ0=sQuery(id+"F0.wireOp",EDGE,"E2.left");var subQ1=sQuery(id+"F0.wireOp",EDGE,"E1");var subQ2=makeQuery(id+"F0.imprint","INTERSECT",VERTEX,{"derivedFrom":[subQ1,subQ0]});Q298=makeQuery(id+"F0.imprint","IMPRINT",FACE,{"disambiguationData":[TD([[makeQuery(id+"F0.imprint","IMPRINT",EDGE,{"disambiguationData":[TD([[subQ2,-1.0]])],"derivedFrom":subQ1}),-1.0]])]});}
            var Q299;
            {var subQ0=sQuery(id+"F0.wireOp",EDGE,"E2.bottom");Q299=makeQuery(id+"F0.imprint","IMPRINT",FACE,{"disambiguationData":[TD([[makeQuery(id+"F0.imprint","IMPRINT",EDGE,{"derivedFrom":subQ0}),1.0]])]});}
            extrude(context, id + "F1", {"entities" : qUnion([Q0, Q1, Q2, Q3, Q4, Q5, Q6, Q7, Q8, Q9, Q10, Q11, Q12, Q13, Q14, Q15, Q16, Q17, Q18, Q19, Q20, Q21, Q22, Q23, Q24, Q25, Q26, Q27, Q28, Q29, Q30, Q31, Q32, Q33, Q34, Q35, Q36, Q37, Q38, Q39, Q40, Q41, Q42, Q43, Q44, Q45, Q46, Q47, Q48, Q49, Q50, Q51, Q52, Q53, Q54, Q55, Q56, Q57, Q58, Q59, Q60, Q61, Q62, Q63, Q64, Q65, Q66, Q67, Q68, Q69, Q70, Q71, Q72, Q73, Q74, Q75, Q76, Q77, Q78, Q79, Q80, Q81, Q82, Q83, Q84, Q85, Q86, Q87, Q88, Q89, Q90, Q91, Q92, Q93, Q94, Q95, Q96, Q97, Q98, Q99, Q100, Q101, Q102, Q103, Q104, Q105, Q106, Q107, Q108, Q109, Q110, Q111, Q112, Q113, Q114, Q115, Q116, Q117, Q118, Q119, Q120, Q121, Q122, Q123, Q124, Q125, Q126, Q127, Q128, Q129, Q130, Q131, Q132, Q133, Q134, Q135, Q136, Q137, Q138, Q139, Q140, Q141, Q142, Q143, Q144, Q145, Q146, Q147, Q148, Q149, Q150, Q151, Q152, Q153, Q154, Q155, Q156, Q157, Q158, Q159, Q160, Q161, Q162, Q163, Q164, Q165, Q166, Q167, Q168, Q169, Q170, Q171, Q172, Q173, Q174, Q175, Q176, Q177, Q178, Q179, Q180, Q181, Q182, Q183, Q184, Q185, Q186, Q187, Q188, Q189, Q190, Q191, Q192, Q193, Q194, Q195, Q196, Q197, Q198, Q199, Q200, Q201, Q202, Q203, Q204, Q205, Q206, Q207, Q208, Q209, Q210, Q211, Q212, Q213, Q214, Q215, Q216, Q217, Q218, Q219, Q220, Q221, Q222, Q223, Q224, Q225, Q226, Q227, Q228, Q229, Q230, Q231, Q232, Q233, Q234, Q235, Q236, Q237, Q238, Q239, Q240, Q241, Q242, Q243, Q244, Q245, Q246, Q247, Q248, Q249, Q250, Q251, Q252, Q253, Q254, Q255, Q256, Q257, Q258, Q259, Q260, Q261, Q262, Q263, Q264, Q265, Q266, Q267, Q268, Q269, Q270, Q271, Q272, Q273, Q274, Q275, Q276, Q277, Q278, Q279, Q280, Q281, Q282, Q283, Q284, Q285, Q286, Q287, Q288, Q289, Q290, Q291, Q292, Q293, Q294, Q295, Q296, Q297, Q298, Q299]), "depth" : 3 * mm, "offsetDistance" : 25 * mm});
        }
    });
